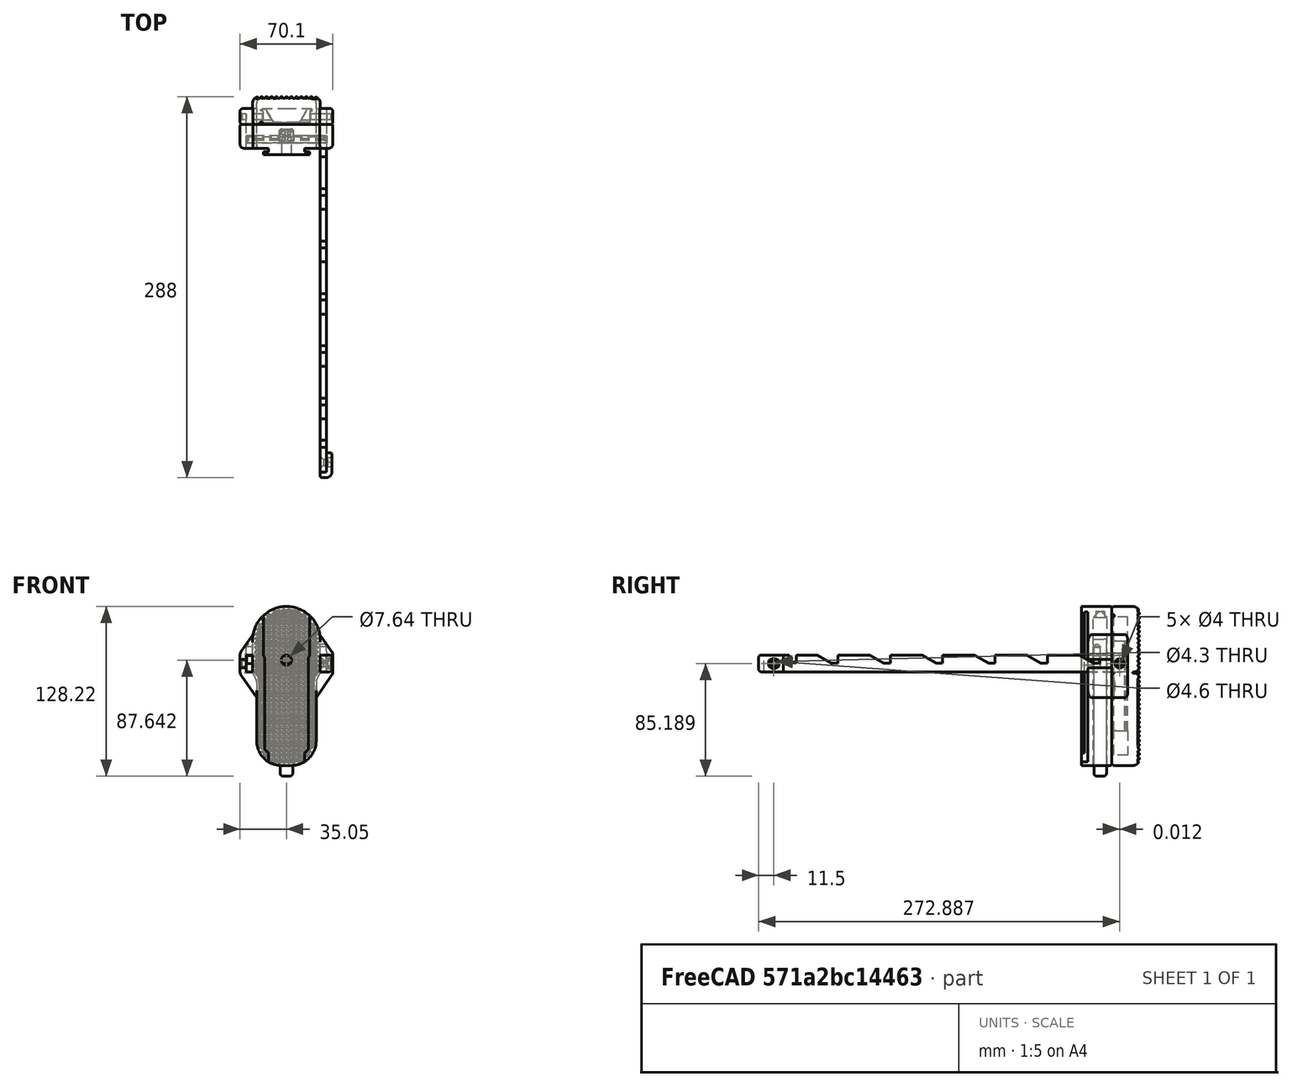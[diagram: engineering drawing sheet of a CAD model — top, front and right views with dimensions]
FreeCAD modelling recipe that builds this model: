
FCSTD DOCUMENT  (FreeCAD 0.19R24291 (Git))
Label: TelescopingButtExtensionMetalArms
License: All rights reserved
LicenseURL: http://en.wikipedia.org/wiki/All_rights_reserved
objects: Sketcher::SketchObject×34, PartDesign::Pocket×20, TechDraw::DrawViewDimension×13, PartDesign::Pad×11, PartDesign::Fillet×10, PartDesign::Body×7, Spreadsheet::Sheet×5, PartDesign::Chamfer×5, PartDesign::Mirrored×4, PartDesign::LinearPattern×3, App::Part×3, Part::Mirroring×2, TechDraw::DrawSVGTemplate×2, TechDraw::DrawViewPart×2, TechDraw::DrawPage×2, PartDesign::SubtractivePipe×1, PartDesign::AdditivePipe×1, PartDesign::Groove×1
note: 148 computed .brp shape members not serialized (recipe doc carries the construction recipe); baked Part::Feature solids carry a one-line shape summary decoded from their .brp

FEATURE [Spreadsheet::Sheet] Spreadsheet  label="P90Measurements"
  cells = A1=ButtDovetail; D1=Overall; G1=ButtPad; I1=Reference Point; J1=Bottom of pad, just at base of dovetail body; L1=SpaceForTelescopingBar; M1(SpaceForTelescopingBar)==0.584"; A2=DovetailHeight; B2(DovetailHeight)==0.192"; D2=ButtOverallHeight; E2(ButtOverallHeight)==4.733"; G2=PadWidestWidth; H2(PadWidestWidth)==2.017"; A3=DovetailBodyWidth; B3(DovetailBodyWidth)==28mm; D3=PadBCGHoleFromReferencePoint; E3(PadBCGHoleFromReferencePoint)==2.997"; G3=PadThinnestWidth; H3(PadThinnestWidth)==1.772"; A4=DovetailLedgeHeight; B4(DovetailLedgeHeight)==0.1"; D4=PadBCGHoleDiameter; E4(PadBCGHoleDiameter)==0.277"; G4=PadWidestWidthInnerShoulderDistanceFromReferencePoint; H4(PadWidestWidthInnerShoulderDistanceFromReferencePoint)==2.532"; A5=DovetailLedgeWidestWidth; B5(DovetailLedgeWidestWidth)==35.5mm; D5=PadBCGHoleDepth; E5(PadBCGHoleDepth)==0.375"; G5=PadWidestWidthOuterShoulderDistanceFromReferencePoint; H5(PadWidestWidthOuterShoulderDistanceFromReferencePoint)==2.785"; A6=DovetailLedgeMiddleWidth; B6(DovetailLedgeMiddleWidth)==1.32"; G6=PadBottomWidth; H6(PadBottomWidth)==0.3"; A7=DovetailMiddleWidthInsideShoulderDistanceFromReferencePoint; B7(DovetailMiddleWidthInsideShoulderDistanceFromReferencePoint)==0.37"; A8=DovetailMiddleWidthOutsideShoulderDistanceFromReferencePoint; B8(DovetailMiddleWidthOutsideShoulderDistanceFromReferencePoint)==0.484"; A9=DovetailBottobBodyBevelDistanceFromReferencePoint; B9(DovetailBottobBodyBevelDistanceFromReferencePoint)==0.154"; A10=DovetailWidestLedgeStartingPointFromReferencePoint; B10(DovetailWidestLedgeStartingPointFromReferencePoint)==3.222"
FEATURE [Spreadsheet::Sheet] Spreadsheet001  label="ProjectSettings"
  cells = A1=Tolerance; A2=LooseTolerance; B2(LooseTolerance)==0.3mm; C2=SpringMaxHeight; D2(SpringMaxHeight)==20mm; E2=CrosspinWidth; F2(CrosspinWidth)==4mm; G2=EndcapScrewBodyDiameter; H2(EndcapScrewBodyDiameter)==4mm; I2=LengthFromButtToChargingHandleShelf; J2(LengthFromButtToChargingHandleShelf)==310mm; K2=AdditionalPrinterTolerance; L2(AdditionalPrinterTolerance)==0mm; A3=TightTolerance; B3(TightTolerance)==0.1mm + AdditionalPrinterTolerance; C3=TelescopingPadOAL; D3(TelescopingPadOAL)==TelescopingBarInsertDepth + TelescopingButtThickness; E3=CrosspinHeight; F3(CrosspinHeight)==6mm; G3=EndcapScrewHeadDiameter; H3(EndcapScrewHeadDiameter)==6mm; A4=WallThickness; B4(WallThickness)==4mm; C4=StandardFillet; D4(StandardFillet)==2mm; E4=CrosspinLength; G4=EndcapNutHeight; H4(EndcapNutHeight)==0.273"; A5=LockingButtonWidth; B5(LockingButtonWidth)==10mm; C5=LockingPinWidth; D5(LockingPinWidth)==0.1875"; E5=ButtonActuationDistance; F5(ButtonActuationDistance)==CrosspinHeight * 2; G5=EndcapNutThickness; H5(EndcapNutThickness)==0.121"; A6=LockingButtonHeight; B6(LockingButtonHeight)==10mm; C6=LockingPinHeight; D6(LockingPinHeight)==6mm; G6=EndcapSectionOnBarLength; H6(EndcapSectionOnBarLength)==15mm; A7=LockingButtonLength; B7(LockingButtonLength)==60mm; C7=LockingPinLength; D7(LockingPinLength)==40mm; G7=EndcapSectionHangingOffOfBarLength; H7(EndcapSectionHangingOffOfBarLength)==WallThickness; A8=LockingButtonHoleDepth; B8(LockingButtonHoleDepth)==<<P90Measurements>>.PadWidestWidthOuterShoulderDistanceFromReferencePoint + BarThickness + LockingPinHeight * 3 + SpringMaxHeight; C8=BarThickness; D8(BarThickness)==0.1875"; G8=ScrewCountersinkDepth; H8(ScrewCountersinkDepth)==0.089"; A9=LockingButtonActuationDistance; B9(LockingButtonActuationDistance)==6mm; C9=BarHeight; D9(BarHeight)==12.7mm; G9=EndcapScrewThreadHeight; H9(EndcapScrewThreadHeight)==8mm; A10=LockingBodyLength; B10(LockingBodyLength)==WallThickness * 2 + LockingButtonHeight; C10=BarLength; D10(BarLength)==275mm; A11=TelescopingPadComfortFilletRadius; B11(TelescopingPadComfortFilletRadius)==5mm; C11=BarNumberOfKnotches; D11(BarNumberOfKnotches)=6; C12=TelescopingBarInsertDepth; D12(TelescopingBarInsertDepth)==WallThickness * 2 + CrosspinWidth; A13=ScallopRadius; B13(ScallopRadius)==1.5mm; C13=TelescopingButtThickness; D13(TelescopingButtThickness)==10mm; A14=DistanceBetweenScallops; B14(DistanceBetweenScallops)==0.25mm; C14=BarDistanceBetweenKnotches; D14(BarDistanceBetweenKnotches)=; C15=BarLastKnotchLocationFromOrigin; D15(BarLastKnotchLocationFromOrigin)==BarLength - EndcapSectionOnBarLength - WallThickness; A16=PaperworkLidNubWidth; B16(PaperworkLidNubWidth)==2mm; C16=BarOccupiedLength; D16(BarOccupiedLength)==WallThickness * 4 + LockingButtonHeight + CrosspinWidth; A17=PaperworkLidNubHeight; B17(PaperworkLidNubHeight)==1.5mm; C17=BarUnoccupiedLength; D17(BarUnoccupiedLength)==BarLength - BarOccupiedLength; A18=PaperworkLidWallThickness; B18(PaperworkLidWallThickness)==2mm; A19=PaperworkLidFingerHoleDiameter; B19(PaperworkLidFingerHoleDiameter)==20mm; A20=PaperworkLipTabWallFilletRadius; B20(PaperworkLipTabWallFilletRadius)==4mm; A21=PaperwokLipInteriorWallAngle; B21(PaperwokLipInteriorWallAngle)=120; A22=PaperworklidbaseThickness; B22(PaperworklidbaseThickness)==1.5mm; A24=LockingButtonHoleClearanceForChamfer; B24(LockingButtonHoleClearanceForChamfer)==min(LockingButtonWidth; LockingButtonHeight) * 9 / 20; A25=LockingPinPocketOverhangCompensationDistance; B25(LockingPinPocketOverhangCompensationDistance)==1.5mm
FEATURE [Sketcher::SketchObject] Sketch  label="DovetailBodySketch"
  FullyConstrained = true
  MapMode = 5
  Placement = pos=(0,0,0) rot=(1,0,0;1.5708rad)
  Support = -> [XZ_Plane]
  expr: Constraints[10] = <<P90Measurements>>.DovetailBodyWidth - <<ProjectSettings>>.LooseTolerance * 2
  expr: Constraints[9] = <<P90Measurements>>.ButtOverallHeight
  sketch-geometry (4):
    g0: LineSegment StartX=-13.7 StartY=120.218 StartZ=0 EndX=13.7 EndY=120.218 EndZ=0
    g1: LineSegment StartX=13.7 StartY=120.218 StartZ=0 EndX=13.7 EndY=0 EndZ=0
    g2: LineSegment StartX=13.7 StartY=0 StartZ=0 EndX=-13.7 EndY=0 EndZ=0
    g3: LineSegment StartX=-13.7 StartY=0 StartZ=0 EndX=-13.7 EndY=120.218 EndZ=0
  constraints (11):
    c: Coincident(g0,g1)
    c: Coincident(g1,g2)
    c: Coincident(g2,g3)
    c: Coincident(g3,g0)
    c: Horizontal(g0)
    c: Vertical(g1)
    c: Vertical(g3)
    c: PointOnObject(g1,g-1)
    c: Symmetric(g1,g2,g-2)
    c: DistanceY(g1,g1) = 120.218
    c: DistanceX(g0,g0) = 27.4
FEATURE [PartDesign::Pad] Pad  label="DovetailBodyPad"
  Direction = (1,1,1)
  Length = 4.8768
  Length2 = 100
  Placement = pos=(0,0,0) rot=(1,0,0;1.5708rad)
  Profile = -> Sketch
  Type = 0
  expr: Length = <<P90Measurements>>.DovetailHeight
FEATURE [Sketcher::SketchObject] Sketch001  label="DovetailLedgeSketch"
  AttachmentOffset = pos=(0,0,4.8768) rot=(0,0,1;0rad)
  FullyConstrained = true
  MapMode = 5
  Placement = pos=(0,-4.8768,-1.1e-15) rot=(1,0,0;1.5708rad)
  Support = -> [XZ_Plane]
  expr: .AttachmentOffset.Base.z = <<P90Measurements>>.DovetailHeight
  expr: Constraints[10] = <<P90Measurements>>.DovetailLedgeWidestWidth - <<ProjectSettings>>.LooseTolerance * 2
  expr: Constraints[9] = <<P90Measurements>>.ButtOverallHeight
  sketch-geometry (4):
    g0: LineSegment StartX=-17.45 StartY=120.218 StartZ=0 EndX=17.45 EndY=120.218 EndZ=0
    g1: LineSegment StartX=17.45 StartY=120.218 StartZ=0 EndX=17.45 EndY=0 EndZ=0
    g2: LineSegment StartX=17.45 StartY=0 StartZ=0 EndX=-17.45 EndY=0 EndZ=0
    g3: LineSegment StartX=-17.45 StartY=0 StartZ=0 EndX=-17.45 EndY=120.218 EndZ=0
  constraints (11):
    c: Coincident(g0,g1)
    c: Coincident(g1,g2)
    c: Coincident(g2,g3)
    c: Coincident(g3,g0)
    c: Horizontal(g0)
    c: Vertical(g1)
    c: Vertical(g3)
    c: PointOnObject(g1,g-1)
    c: Symmetric(g2,g1,g-2)
    c: DistanceY(g1,g1) = 120.218
    c: DistanceX(g0,g0) = 34.9
FEATURE [PartDesign::Pad] Pad001  label="DovetailLedgePad"
  BaseFeature = -> Pad
  Direction = (1,1,1)
  Length = 2.24
  Length2 = 100
  Placement = pos=(0,0,0) rot=(1,0,0;1.5708rad)
  Profile = -> Sketch001
  Refine = true
  Reversed = true
  Type = 0
  expr: Length = <<P90Measurements>>.DovetailLedgeHeight - <<ProjectSettings>>.LooseTolerance
FEATURE [Sketcher::SketchObject] Sketch002  label="DovetailLedgeCutSketch"
  FullyConstrained = true
  MapMode = 5
  Placement = pos=(0,0,0) rot=(1,0,0;1.5708rad)
  Support = -> [XZ_Plane]
  expr: Constraints[35] = <<P90Measurements>>.DovetailMiddleWidthOutsideShoulderDistanceFromReferencePoint
  expr: Constraints[33] = <<P90Measurements>>.DovetailLedgeMiddleWidth - <<ProjectSettings>>.LooseTolerance * 2
  expr: Constraints[36] = <<P90Measurements>>.DovetailWidestLedgeStartingPointFromReferencePoint
  expr: Constraints[34] = <<P90Measurements>>.DovetailMiddleWidthInsideShoulderDistanceFromReferencePoint
  expr: Constraints[32] = <<P90Measurements>>.DovetailBodyWidth - <<ProjectSettings>>.LooseTolerance * 2
  expr: Constraints[29] = <<P90Measurements>>.DovetailLedgeWidestWidth - <<ProjectSettings>>.LooseTolerance * 2
  expr: Constraints[28] = <<P90Measurements>>.ButtOverallHeight
  sketch-geometry (16):
    g0: LineSegment StartX=-27.45 StartY=130.218 StartZ=0 EndX=27.45 EndY=130.218 EndZ=0
    g1: LineSegment StartX=27.45 StartY=130.218 StartZ=0 EndX=27.45 EndY=-10 EndZ=0
    g2: LineSegment StartX=27.45 StartY=-10 StartZ=0 EndX=-27.45 EndY=-10 EndZ=0
    g3: LineSegment StartX=-27.45 StartY=-10 StartZ=0 EndX=-27.45 EndY=130.218 EndZ=0
    g4: LineSegment StartX=-13.7 StartY=0 StartZ=0 EndX=13.7 EndY=0 EndZ=0
    g5: LineSegment StartX=13.7 StartY=0 StartZ=0 EndX=13.7 EndY=9.398 EndZ=0
    g6: LineSegment StartX=13.7 StartY=9.398 StartZ=0 EndX=16.464 EndY=12.2936 EndZ=0
    g7: LineSegment StartX=16.464 StartY=12.2936 StartZ=0 EndX=16.464 EndY=81.8388 EndZ=0
    g8: LineSegment StartX=16.464 StartY=81.8388 StartZ=0 EndX=17.45 EndY=82.8598 EndZ=0
    g9: LineSegment StartX=17.45 StartY=82.8598 StartZ=0 EndX=17.45 EndY=120.218 EndZ=0
    g10: LineSegment StartX=17.45 StartY=120.218 StartZ=0 EndX=-17.45 EndY=120.218 EndZ=0
    g11: LineSegment StartX=-17.45 StartY=120.218 StartZ=0 EndX=-17.45 EndY=82.8598 EndZ=0
    g12: LineSegment StartX=-17.45 StartY=82.8598 StartZ=0 EndX=-16.464 EndY=81.8388 EndZ=0
    g13: LineSegment StartX=-16.464 StartY=81.8388 StartZ=0 EndX=-16.464 EndY=12.2936 EndZ=0
    g14: LineSegment StartX=-16.464 StartY=12.2936 StartZ=0 EndX=-13.7 EndY=9.398 EndZ=0
    g15: LineSegment StartX=-13.7 StartY=9.398 StartZ=0 EndX=-13.7 EndY=0 EndZ=0
  constraints (44):
    c: Coincident(g0,g1)
    c: Coincident(g1,g2)
    c: Coincident(g2,g3)
    c: Coincident(g3,g0)
    c: Horizontal(g0)
    c: Horizontal(g2)
    c: Vertical(g1)
    c: Vertical(g3)
    c: PointOnObject(g4,g-1)
    c: Coincident(g4,g5)
    c: Vertical(g5)
    c: Coincident(g5,g6)
    c: Coincident(g6,g7)
    c: Vertical(g7)
    c: Coincident(g7,g8)
    c: Coincident(g8,g9)
    c: Vertical(g9)
    c: Coincident(g9,g10)
    c: Coincident(g10,g11)
    c: Coincident(g11,g12)
    c: Coincident(g12,g13)
    c: Vertical(g13)
    c: Coincident(g13,g14)
    c: Coincident(g14,g15)
    c: Coincident(g15,g4)
    c: Vertical(g15)
    c: Horizontal(g14,g5)
    c: Horizontal(g13,g6)
    c: DistanceY(g4,g9) = 120.218
    c: DistanceX(g10,g10) = 34.9
    c: Symmetric(g10,g9,g-2)
    c: Symmetric(g12,g7,g-2)
    c: DistanceX(g4,g4) = 27.4
    c: DistanceX(g12,g7) = 32.928
    c: DistanceY(g14) = 9.398
    c: DistanceY(g4,g13) = 12.2936
    c: DistanceY(g-1,g7) = 81.8388
    c: DistanceY(g10,g0) = 10
    c: DistanceX(g0,g10) = 10
    c: DistanceX(g9,g1) = 10
    c: DistanceY(g1,g4) = 10
    c: Symmetric(g4,g4,g-2)
    c: Symmetric(g8,g11,g-2)
    c: Angle(g12,g13) = 2.37365
FEATURE [PartDesign::Pocket] Pocket  label="DovetailLedgeCutPocket"
  BaseFeature = -> Pad001
  Length = 5
  Length2 = 100
  Placement = pos=(0,0,0) rot=(1,0,0;1.5708rad)
  Profile = -> Sketch002
  Reversed = true
  Type = 1
FEATURE [Sketcher::SketchObject] Sketch003  label="PadBodySketch"
  FullyConstrained = true
  MapMode = 5
  Placement = pos=(0,0,0) rot=(1,0,0;1.5708rad)
  Support = -> [XZ_Plane]
  expr: Constraints[27] = <<P90Measurements>>.PadWidestWidthInnerShoulderDistanceFromReferencePoint
  expr: Constraints[22] = <<P90Measurements>>.PadWidestWidthOuterShoulderDistanceFromReferencePoint
  expr: Constraints[19] = <<P90Measurements>>.PadThinnestWidth
  expr: Constraints[21] = <<P90Measurements>>.PadWidestWidth
  expr: Constraints[20] = <<P90Measurements>>.ButtOverallHeight
  sketch-geometry (12):
    g0: LineSegment StartX=-22.5044 StartY=0 StartZ=0 EndX=22.5044 EndY=0 EndZ=0
    g1: LineSegment StartX=22.5044 StartY=0 StartZ=0 EndX=22.5044 EndY=63.2152 EndZ=0
    g2: LineSegment StartX=-22.5044 StartY=63.2152 StartZ=0 EndX=-22.5044 EndY=0 EndZ=0
    g3: LineSegment StartX=-25.6159 StartY=120.218 StartZ=0 EndX=25.6159 EndY=120.218 EndZ=0
    g4: LineSegment StartX=25.6159 StartY=120.218 StartZ=0 EndX=25.6159 EndY=70.739 EndZ=0
    g5: LineSegment StartX=-25.6159 StartY=70.739 StartZ=0 EndX=-25.6159 EndY=120.218 EndZ=0
    g6: LineSegment StartX=-25.3621 StartY=69.6414 StartZ=0 EndX=-22.7582 EndY=64.3128 EndZ=0
    g7: LineSegment StartX=25.3621 StartY=69.6414 StartZ=0 EndX=22.7582 EndY=64.3128 EndZ=0
    g8: ArcOfCircle CenterX=-23.1159 CenterY=70.739 CenterZ=0 NormalX=0 NormalY=0 NormalZ=1 AngleXU=0 Radius=2.5 StartAngle=3.14159 EndAngle=3.59612
    g9: ArcOfCircle CenterX=-25.0044 CenterY=63.2152 CenterZ=0 NormalX=0 NormalY=0 NormalZ=1 AngleXU=0 Radius=2.5 StartAngle=2e-16 EndAngle=0.454529
    g10: ArcOfCircle CenterX=23.1159 CenterY=70.739 CenterZ=0 NormalX=0 NormalY=0 NormalZ=1 AngleXU=0 Radius=2.5 StartAngle=5.82866 EndAngle=6.28319
    g11: ArcOfCircle CenterX=25.0044 CenterY=63.2152 CenterZ=0 NormalX=0 NormalY=0 NormalZ=1 AngleXU=0 Radius=2.5 StartAngle=2.68706 EndAngle=3.14159
  constraints (28):
    c: Coincident(g0,g1)
    c: Coincident(g2,g0)
    c: Vertical(g1)
    c: Vertical(g2)
    c: PointOnObject(g0,g-1)
    c: Coincident(g3,g4)
    c: Coincident(g5,g3)
    c: Vertical(g4)
    c: Vertical(g5)
    c: Tangent(g8,g5) = 1.5708
    c: Tangent(g8,g6) = -1.5708
    c: Tangent(g9,g6) = 1.5708
    c: Tangent(g11,g1) = 1.5708
    c: Tangent(g11,g7) = -1.5708
    c: Tangent(g7,g10) = 1.5708
    c: Tangent(g10,g4) = 1.5708
    c: Tangent(g9,g2) = 1.5708
    c: Symmetric(g0,g0,g-2)
    c: Symmetric(g3,g3,g-2)
    c: DistanceX(g0,g0) = 45.0088
    c: DistanceY(g0,g3) = 120.218
    c: DistanceX(g3,g3) = 51.2318
    c: DistanceY(g-1,g8) = 70.739
    c: Symmetric(g7,g6,g-2)
    c: Symmetric(g6,g7,g-2)
    c: Equal(g11,g10)
    c: Diameter(g11) = 5
    c: DistanceY(g6) = 64.3128
FEATURE [PartDesign::Pad] Pad002  label="PadBodyPad"
  BaseFeature = -> Pocket
  Direction = (1,1,1)
  Length = 18
  Length2 = 100
  Placement = pos=(0,0,0) rot=(1,0,0;1.5708rad)
  Profile = -> Sketch003
  Reversed = true
  Type = 0
  expr: Length = <<ProjectSettings>>.WallThickness * 2 + <<ProjectSettings>>.LockingButtonHeight
FEATURE [Sketcher::SketchObject] Sketch004  label="PadBevelsCutSketch"
  FullyConstrained = true
  MapMode = 5
  Placement = pos=(0,0,0) rot=(1,0,0;1.5708rad)
  Support = -> [XZ_Plane]
  expr: Constraints[32] = <<P90Measurements>>.PadBottomWidth
  expr: Constraints[29] = <<P90Measurements>>.PadWidestWidth
  expr: Constraints[31] = <<P90Measurements>>.PadWidestWidthInnerShoulderDistanceFromReferencePoint - 5mm
  expr: Constraints[30] = <<P90Measurements>>.PadThinnestWidth
  expr: Constraints[27] = <<P90Measurements>>.ButtOverallHeight
  sketch-geometry (15):
    g0: LineSegment StartX=-35.6159 StartY=130.218 StartZ=0 EndX=35.6159 EndY=130.218 EndZ=0
    g1: LineSegment StartX=35.6159 StartY=130.218 StartZ=0 EndX=35.6159 EndY=-10 EndZ=0
    g2: LineSegment StartX=35.6159 StartY=-10 StartZ=0 EndX=-35.6159 EndY=-10 EndZ=0
    g3: LineSegment StartX=-35.6159 StartY=-10 StartZ=0 EndX=-35.6159 EndY=130.218 EndZ=0
    g4: ArcOfCircle CenterX=-3.81 CenterY=18.6944 CenterZ=0 NormalX=0 NormalY=0 NormalZ=1 AngleXU=0 Radius=18.6944 StartAngle=3.14159 EndAngle=4.71239
    g5: ArcOfCircle CenterX=3.81 CenterY=18.6944 CenterZ=0 NormalX=0 NormalY=0 NormalZ=1 AngleXU=0 Radius=18.6944 StartAngle=4.71239 EndAngle=6.28319
    g6: ArcOfCircle CenterX=2.5e-15 CenterY=94.6023 CenterZ=0 NormalX=0 NormalY=0 NormalZ=1 AngleXU=0 Radius=25.6159 StartAngle=1.5708 EndAngle=3.14159
    g7: ArcOfCircle CenterX=2.5e-15 CenterY=94.6023 CenterZ=0 NormalX=0 NormalY=0 NormalZ=1 AngleXU=0 Radius=25.6159 StartAngle=0 EndAngle=1.5708
    g8: LineSegment StartX=-25.6159 StartY=94.6023 StartZ=0 EndX=-25.6159 EndY=59.3128 EndZ=0
    g9: LineSegment StartX=-25.6159 StartY=59.3128 StartZ=0 EndX=-22.5044 EndY=59.3128 EndZ=0
    g10: LineSegment StartX=-22.5044 StartY=59.3128 StartZ=0 EndX=-22.5044 EndY=18.6944 EndZ=0
    g11: LineSegment StartX=-3.81 StartY=0 StartZ=0 EndX=3.81 EndY=0 EndZ=0
    g12: LineSegment StartX=22.5044 StartY=18.6944 StartZ=0 EndX=22.5044 EndY=59.3128 EndZ=0
    g13: LineSegment StartX=22.5044 StartY=59.3128 StartZ=0 EndX=25.6159 EndY=59.3128 EndZ=0
    g14: LineSegment StartX=25.6159 StartY=59.3128 StartZ=0 EndX=25.6159 EndY=94.6023 EndZ=0
  constraints (39):
    c: Coincident(g0,g1)
    c: Coincident(g1,g2)
    c: Coincident(g2,g3)
    c: Coincident(g3,g0)
    c: Horizontal(g0)
    c: Vertical(g1)
    c: Vertical(g3)
    c: Symmetric(g2,g1,g-2)
    c: PointOnObject(g4,g-1)
    c: PointOnObject(g5,g-1)
    c: Vertical(g8)
    c: Coincident(g9,g8)
    c: Vertical(g10)
    c: Vertical(g12)
    c: Coincident(g13,g12)
    c: Vertical(g14)
    c: Coincident(g13,g14)
    c: Horizontal(g13)
    c: Tangent(g6,g8) = -1.5708
    c: Tangent(g7,g14) = -1.5708
    c: Tangent(g10,g4) = -1.5708
    c: Tangent(g11,g4) = -1.5708
    c: Tangent(g11,g5) = -1.5708
    c: Tangent(g12,g5) = -1.5708
    c: Symmetric(g12,g10,g-2)
    c: Symmetric(g8,g13,g-2)
    c: Coincident(g10,g9)
    c: DistanceY(g-1,g7) = 120.218
    c: Equal(g5,g4)
    c: DistanceX(g6,g7) = 51.2318
    c: DistanceX(g9,g12) = 45.0088
    c: DistanceY(g-1,g12) = 59.3128
    c: DistanceX(g11,g11) = 7.62
    c: PointOnObject(g6,g-2)
    c: Tangent(g6,g7) = -1.5708
    c: Equal(g8,g14)
    c: DistanceY(g2,g-1) = 10
    c: DistanceY(g6,g0) = 10
    c: DistanceX(g7,g1) = 10
FEATURE [PartDesign::Pocket] Pocket001  label="PadBevelsCutPocket"
  BaseFeature = -> Pad002
  Length = 5
  Length2 = 100
  Midplane = true
  Placement = pos=(0,0,0) rot=(1,0,0;1.5708rad)
  Profile = -> Sketch004
  Type = 1
FEATURE [Spreadsheet::Sheet] Spreadsheet002  label="TelescopingBarSettings"
  cells = A1=BarOffsetFromCenter; B1(BarOffsetFromCenter)==<<PadBodyPad>>.Length + <<TelescoptingPadBodyPad>>.Length; A2=LengthFromButtToChargingHandleShelf; B2(LengthFromButtToChargingHandleShelf)==310mm; A3=BarLength; B3(BarLength)==270mm; A4=BarThickness; B4(BarThickness)==0.125"; A5=CrosspinThickness; B5(CrosspinThickness)==0.125"; A6=BarHeight; B6(BarHeight)==12.7mm; A7=LockingPinThickness; B7(LockingPinThickness)==0.125"; A8=BarNumberOfKnotches; B8(BarNumberOfKnotches)=6; A9=ScrewCountersinkDepth; B9(ScrewCountersinkDepth)==0.089"; A10=EndcapHexnutHeight; B10(EndcapHexnutHeight)==0.273"; A11=EndcapHexnutThickness; B11(EndcapHexnutThickness)==0.121"; A12=CrosspinHeight; B12(CrosspinHeight)==6mm; A13=LockingPinHeight; B13(LockingPinHeight)==6mm
FEATURE [Sketcher::SketchObject] Sketch008  label="TelescoptingPadBodySketch"
  FullyConstrained = true
  MapMode = 5
  Placement = pos=(0,0,0) rot=(1,0,0;1.5708rad)
  Support = -> [XZ_Plane002]
  expr: Constraints[20] = <<P90Measurements>>.ButtOverallHeight
  expr: Constraints[21] = <<P90Measurements>>.PadWidestWidth
  expr: Constraints[19] = <<P90Measurements>>.PadThinnestWidth
  expr: Constraints[22] = <<P90Measurements>>.PadWidestWidthOuterShoulderDistanceFromReferencePoint
  expr: Constraints[27] = <<P90Measurements>>.PadWidestWidthInnerShoulderDistanceFromReferencePoint
  sketch-geometry (12):
    g0: LineSegment StartX=-22.5044 StartY=0 StartZ=0 EndX=22.5044 EndY=0 EndZ=0
    g1: LineSegment StartX=22.5044 StartY=0 StartZ=0 EndX=22.5044 EndY=63.2152 EndZ=0
    g2: LineSegment StartX=-22.5044 StartY=63.2152 StartZ=0 EndX=-22.5044 EndY=0 EndZ=0
    g3: LineSegment StartX=-25.6159 StartY=120.218 StartZ=0 EndX=25.6159 EndY=120.218 EndZ=0
    g4: LineSegment StartX=25.6159 StartY=120.218 StartZ=0 EndX=25.6159 EndY=70.739 EndZ=0
    g5: LineSegment StartX=-25.6159 StartY=70.739 StartZ=0 EndX=-25.6159 EndY=120.218 EndZ=0
    g6: LineSegment StartX=-25.3621 StartY=69.6414 StartZ=0 EndX=-22.7582 EndY=64.3128 EndZ=0
    g7: LineSegment StartX=25.3621 StartY=69.6414 StartZ=0 EndX=22.7582 EndY=64.3128 EndZ=0
    g8: ArcOfCircle CenterX=-23.1159 CenterY=70.739 CenterZ=0 NormalX=0 NormalY=0 NormalZ=1 AngleXU=0 Radius=2.5 StartAngle=3.14159 EndAngle=3.59612
    g9: ArcOfCircle CenterX=-25.0044 CenterY=63.2152 CenterZ=0 NormalX=0 NormalY=0 NormalZ=1 AngleXU=0 Radius=2.5 StartAngle=0 EndAngle=0.454529
    g10: ArcOfCircle CenterX=23.1159 CenterY=70.739 CenterZ=0 NormalX=0 NormalY=0 NormalZ=1 AngleXU=0 Radius=2.5 StartAngle=5.82866 EndAngle=6.28319
    g11: ArcOfCircle CenterX=25.0044 CenterY=63.2152 CenterZ=0 NormalX=0 NormalY=0 NormalZ=1 AngleXU=0 Radius=2.5 StartAngle=2.68706 EndAngle=3.14159
  constraints (29):
    c: Coincident(g0,g1)
    c: Coincident(g2,g0)
    c: Vertical(g1)
    c: Vertical(g2)
    c: PointOnObject(g0,g-1)
    c: Coincident(g3,g4)
    c: Coincident(g5,g3)
    c: Vertical(g4)
    c: Vertical(g5)
    c: Tangent(g8,g5) = 1.5708
    c: Tangent(g8,g6) = -1.5708
    c: Tangent(g9,g6) = 1.5708
    c: Tangent(g11,g1) = 1.5708
    c: Tangent(g11,g7) = -1.5708
    c: Tangent(g7,g10) = 1.5708
    c: Tangent(g10,g4) = 1.5708
    c: Tangent(g9,g2) = 1.5708
    c: Symmetric(g0,g0,g-2)
    c: Symmetric(g3,g3,g-2)
    c: DistanceX(g0,g0) = 45.0088
    c: DistanceY(g0,g3) = 120.218
    c: DistanceX(g3,g3) = 51.2318
    c: DistanceY(g-1,g8) = 70.739
    c: Symmetric(g7,g6,g-2)
    c: Symmetric(g6,g7,g-2)
    c: Equal(g11,g10)
    c: Diameter(g11) = 5
    c: DistanceY(g6) = 64.3128
    c: Angle(g1,g7) = 2.68706  'PadAngle'
FEATURE [PartDesign::Pad] Pad006  label="TelescoptingPadBodyPad"
  Direction = (1,1,1)
  Length = 21
  Length2 = 100
  Placement = pos=(0,0,0) rot=(1,0,0;1.5708rad)
  Profile = -> Sketch008
  Reversed = true
  Type = 0
  expr: Length = <<ProjectSettings>>.TelescopingBarInsertDepth + <<ProjectSettings>>.WallThickness + <<ProjectSettings>>.TelescopingPadComfortFilletRadius
FEATURE [Sketcher::SketchObject] Sketch009  label="TelescopingPadBevelsCutSketch"
  FullyConstrained = true
  MapMode = 5
  Placement = pos=(0,0,0) rot=(1,0,0;1.5708rad)
  Support = -> [XZ_Plane002]
  expr: Constraints[27] = <<P90Measurements>>.ButtOverallHeight
  expr: Constraints[30] = <<P90Measurements>>.PadThinnestWidth
  expr: Constraints[31] = <<P90Measurements>>.PadWidestWidthInnerShoulderDistanceFromReferencePoint - 5mm
  expr: Constraints[29] = <<P90Measurements>>.PadWidestWidth
  expr: Constraints[32] = <<P90Measurements>>.PadBottomWidth
  sketch-geometry (15):
    g0: LineSegment StartX=-35.6159 StartY=130.218 StartZ=0 EndX=35.6159 EndY=130.218 EndZ=0
    g1: LineSegment StartX=35.6159 StartY=130.218 StartZ=0 EndX=35.6159 EndY=-10 EndZ=0
    g2: LineSegment StartX=35.6159 StartY=-10 StartZ=0 EndX=-35.6159 EndY=-10 EndZ=0
    g3: LineSegment StartX=-35.6159 StartY=-10 StartZ=0 EndX=-35.6159 EndY=130.218 EndZ=0
    g4: ArcOfCircle CenterX=-3.81 CenterY=18.6944 CenterZ=0 NormalX=0 NormalY=0 NormalZ=1 AngleXU=0 Radius=18.6944 StartAngle=3.14159 EndAngle=4.71239
    g5: ArcOfCircle CenterX=3.81 CenterY=18.6944 CenterZ=0 NormalX=0 NormalY=0 NormalZ=1 AngleXU=0 Radius=18.6944 StartAngle=4.71239 EndAngle=6.28319
    g6: ArcOfCircle CenterX=8e-16 CenterY=94.6023 CenterZ=0 NormalX=0 NormalY=0 NormalZ=1 AngleXU=0 Radius=25.6159 StartAngle=1.5708 EndAngle=3.14159
    g7: ArcOfCircle CenterX=8e-16 CenterY=94.6023 CenterZ=0 NormalX=0 NormalY=0 NormalZ=1 AngleXU=0 Radius=25.6159 StartAngle=0 EndAngle=1.5708
    g8: LineSegment StartX=-25.6159 StartY=94.6023 StartZ=0 EndX=-25.6159 EndY=59.3128 EndZ=0
    g9: LineSegment StartX=-25.6159 StartY=59.3128 StartZ=0 EndX=-22.5044 EndY=59.3128 EndZ=0
    g10: LineSegment StartX=-22.5044 StartY=59.3128 StartZ=0 EndX=-22.5044 EndY=18.6944 EndZ=0
    g11: LineSegment StartX=-3.81 StartY=0 StartZ=0 EndX=3.81 EndY=0 EndZ=0
    g12: LineSegment StartX=22.5044 StartY=18.6944 StartZ=0 EndX=22.5044 EndY=59.3128 EndZ=0
    g13: LineSegment StartX=22.5044 StartY=59.3128 StartZ=0 EndX=25.6159 EndY=59.3128 EndZ=0
    g14: LineSegment StartX=25.6159 StartY=59.3128 StartZ=0 EndX=25.6159 EndY=94.6023 EndZ=0
  constraints (39):
    c: Coincident(g0,g1)
    c: Coincident(g1,g2)
    c: Coincident(g2,g3)
    c: Coincident(g3,g0)
    c: Horizontal(g0)
    c: Vertical(g1)
    c: Vertical(g3)
    c: Symmetric(g2,g1,g-2)
    c: PointOnObject(g4,g-1)
    c: PointOnObject(g5,g-1)
    c: Vertical(g8)
    c: Coincident(g9,g8)
    c: Vertical(g10)
    c: Vertical(g12)
    c: Coincident(g13,g12)
    c: Vertical(g14)
    c: Coincident(g13,g14)
    c: Horizontal(g13)
    c: Tangent(g6,g8) = -1.5708
    c: Tangent(g7,g14) = -1.5708
    c: Tangent(g10,g4) = -1.5708
    c: Tangent(g11,g4) = -1.5708
    c: Tangent(g11,g5) = -1.5708
    c: Tangent(g12,g5) = -1.5708
    c: Symmetric(g12,g10,g-2)
    c: Symmetric(g8,g13,g-2)
    c: Coincident(g10,g9)
    c: DistanceY(g-1,g7) = 120.218
    c: Equal(g5,g4)
    c: DistanceX(g6,g7) = 51.2318
    c: DistanceX(g9,g12) = 45.0088
    c: DistanceY(g-1,g12) = 59.3128
    c: DistanceX(g11,g11) = 7.62
    c: PointOnObject(g6,g-2)
    c: Tangent(g6,g7) = -1.5708
    c: Equal(g8,g14)
    c: DistanceY(g2,g-1) = 10
    c: DistanceY(g6,g0) = 10
    c: DistanceX(g7,g1) = 10
FEATURE [PartDesign::Pocket] Pocket002  label="TelescopingPadBevelsCutPocket"
  BaseFeature = -> Pad006
  Length = 5
  Length2 = 100
  Midplane = true
  Placement = pos=(0,0,0) rot=(1,0,0;1.5708rad)
  Profile = -> Sketch009
  Type = 1
FEATURE [Sketcher::SketchObject] Sketch010  label="TelescopingBarInsertArmSketch"
  FullyConstrained = true
  MapMode = 5
  Placement = pos=(0,0,0) rot=(1,0,0;1.5708rad)
  Support = -> [XZ_Plane002]
  expr: Constraints[15] = <<P90Measurements>>.PadThinnestWidth / 2
  expr: Constraints[13] = <<ProjectSettings>>.BarHeight + <<ProjectSettings>>.TightTolerance
  expr: Constraints[10] = <<P90Measurements>>.PadWidestWidth / 2
  expr: Constraints[12] = <<P90Measurements>>.PadWidestWidthOuterShoulderDistanceFromReferencePoint
  expr: Constraints[11] = <<ProjectSettings>>.BarThickness + <<ProjectSettings>>.TightTolerance
  sketch-geometry (10):
    g0: LineSegment StartX=30.4784 StartY=70.739 StartZ=0 EndX=30.4784 EndY=83.539 EndZ=0
    g1: LineSegment StartX=30.4784 StartY=83.539 StartZ=0 EndX=25.6159 EndY=83.539 EndZ=0
    g2: LineSegment StartX=25.6159 StartY=83.539 StartZ=0 EndX=25.6159 EndY=70.739 EndZ=0
    g3: LineSegment StartX=25.6159 StartY=70.739 StartZ=0 EndX=30.4784 EndY=70.739 EndZ=0
    g4: LineSegment StartX=35.0484 StartY=70.739 StartZ=0 EndX=35.0484 EndY=83.639 EndZ=0
    g5: LineSegment StartX=22.5044 StartY=102.995 StartZ=0 EndX=22.5044 EndY=51.3834 EndZ=0
    g6: ArcOfCircle CenterX=30.4784 CenterY=70.739 CenterZ=0 NormalX=0 NormalY=0 NormalZ=1 AngleXU=0 Radius=4.57 StartAngle=5.67232 EndAngle=6.28319
    g7: LineSegment StartX=22.5044 StartY=51.3834 StartZ=0 EndX=34.2219 EndY=68.1178 EndZ=0
    g8: LineSegment StartX=22.5044 StartY=102.995 StartZ=0 EndX=34.2219 EndY=86.2602 EndZ=0
    g9: ArcOfCircle CenterX=30.4784 CenterY=83.639 CenterZ=0 NormalX=0 NormalY=0 NormalZ=1 AngleXU=0 Radius=4.57 StartAngle=-9e-16 EndAngle=0.610865
  constraints (28):
    c: Vertical(g0)
    c: Coincident(g0,g1)
    c: Horizontal(g1)
    c: Coincident(g1,g2)
    c: Vertical(g2)
    c: Coincident(g2,g3)
    c: Coincident(g3,g0)
    c: Vertical(g5)
    c: Vertical(g4)
    c: Horizontal(g3)
    c: DistanceX(g-1,g2) = 25.6159
    c: DistanceX(g1,g1) = 4.8625
    c: DistanceY(g-1,g2) = 70.739
    c: DistanceY(g0,g0) = 12.8
    c: Coincident(g6,g0)
    c: DistanceX(g-1,g5) = 22.5044
    c: Coincident(g7,g5)
    c: Coincident(g8,g5)
    c: Tangent(g6,g4) = -1.5708
    c: Tangent(g7,g6) = -1.5708
    c: Equal(g7,g8)
    c: Angle(g4,g7) = 2.53073
    c: DistanceX(g-1,g4) = 35.0484  'DistanceFromCenterlineToOutsideOfBarInsertArm'
    c: PointOnObject(g9,g0)
    c: DistanceY(g0,g9) = 0.1
    c: Tangent(g9,g8) = 1.5708
    c: Tangent(g9,g4) = -1.5708
    c: Diameter(g9) = 9.14
FEATURE [Spreadsheet::Sheet] Spreadsheet003  label="TelescopingPadSettings"
  cells = A1=TelescopingBarInsertDepth; B1(TelescopingBarInsertDepth)==<<ProjectSettings>>.WallThickness * 2 + <<TelescopingBarSettings>>.CrosspinThickness + <<ProjectSettings>>.TightTolerance * 2; A2=TelescopingButtThickness; B2(TelescopingButtThickness)==10mm; A3=TelescopingPadOAL; B3(TelescopingPadOAL)==TelescopingBarInsertDepth + TelescopingButtThickness
FEATURE [PartDesign::Pad] Pad007  label="TelescopingBarInsertArmPad"
  BaseFeature = -> Pocket002
  Direction = (1,1,1)
  Length = 12
  Length2 = 100
  Placement = pos=(0,0,0) rot=(1,0,0;1.5708rad)
  Profile = -> Sketch010
  Reversed = true
  Type = 0
  expr: Length = <<ProjectSettings>>.TelescopingBarInsertDepth
FEATURE [Sketcher::SketchObject] Sketch011  label="CrosspinHoleSketch"
  FullyConstrained = true
  MapMode = 5
  Placement = pos=(0,0,0) rot=(0.57735,0.57735,0.57735;2.0944rad)
  Support = -> [YZ_Plane002]
  expr: Constraints[2] = <<ProjectSettings>>.CrosspinWidth
  expr: Constraints[0] = <<P90Measurements>>.PadWidestWidthOuterShoulderDistanceFromReferencePoint + <<ProjectSettings>>.BarHeight / 2 + <<ProjectSettings>>.TightTolerance
  expr: Constraints[1] = <<TelescopingPadSettings>>.TelescopingBarInsertDepth / 2 + <<ProjectSettings>>.TightTolerance * 2
  sketch-geometry (1):
    g0: Circle CenterX=5.8875 CenterY=77.189 CenterZ=0 NormalX=0 NormalY=0 NormalZ=1 AngleXU=0 Radius=2
  constraints (3):
    c: DistanceY(g-1,g0) = 77.189
    c: DistanceX(g-1,g0) = 5.8875
    c: Diameter(g0) = 4
FEATURE [PartDesign::Mirrored] Mirrored  label="TelescopingBarInsertArmMirror"
  BaseFeature = -> Pad007
  MirrorPlane = -> Sketch010 [V_Axis]
  Originals = -> [Pad007]
  Placement = pos=(0,0,0) rot=(1,0,0;1.5708rad)
FEATURE [PartDesign::Pocket] Pocket003  label="CrosspinHolePocket"
  BaseFeature = -> Mirrored
  Length = 5
  Length2 = 100
  Midplane = true
  Placement = pos=(0,0,0) rot=(1,0,0;1.5708rad)
  Profile = -> Sketch011
  Type = 1
FEATURE [PartDesign::Fillet] Fillet  label="ComfortFillet"
  Base = -> Pocket003 [Edge59]
  BaseFeature = -> Pocket003
  Placement = pos=(0,0,0) rot=(1,0,0;1.5708rad)
  Radius = 5
  SupportTransform = false
  expr: Radius = <<ProjectSettings>>.TelescopingPadComfortFilletRadius
FEATURE [Spreadsheet::Sheet] Spreadsheet004  label="CentralPadSettings"
  cells = A1=PadThickness; B1(PadThickness)==<<PadBodyPad>>.Length; A2=LockingButtonHoleDepth; B2(LockingButtonHoleDepth)==<<P90Measurements>>.PadWidestWidthOuterShoulderDistanceFromReferencePoint + <<TelescopingBarSettings>>.BarThickness + <<TelescopingBarSettings>>.LockingPinHeight * 3 + SpringMaxHeight; A3=SpringMaxHeight; B3(SpringMaxHeight)==20mm
FEATURE [Sketcher::SketchObject] Sketch014  label="CentralPadTelescopingBarInsertArmSketch"
  FullyConstrained = true
  MapMode = 5
  Placement = pos=(0,0,0) rot=(1,0,0;1.5708rad)
  Support = -> [XZ_Plane]
  expr: Constraints[11] = <<ProjectSettings>>.BarThickness + <<ProjectSettings>>.TightTolerance
  expr: Constraints[12] = <<P90Measurements>>.PadWidestWidthOuterShoulderDistanceFromReferencePoint
  expr: Constraints[10] = <<P90Measurements>>.PadWidestWidth / 2
  expr: Constraints[13] = <<ProjectSettings>>.BarHeight + <<ProjectSettings>>.TightTolerance
  expr: Constraints[16] = <<P90Measurements>>.PadThinnestWidth / 2
  expr: Constraints[34] = <<ProjectSettings>>.LockingPinHeight + <<ProjectSettings>>.TightTolerance * 2
  sketch-geometry (14):
    g0: LineSegment StartX=30.4784 StartY=70.739 StartZ=0 EndX=30.4784 EndY=74.039 EndZ=0
    g1: LineSegment StartX=30.4784 StartY=83.539 StartZ=0 EndX=25.6159 EndY=83.539 EndZ=0
    g2: LineSegment StartX=25.6159 StartY=83.539 StartZ=0 EndX=25.6159 EndY=70.739 EndZ=0
    g3: LineSegment StartX=25.6159 StartY=70.739 StartZ=0 EndX=30.4784 EndY=70.739 EndZ=0
    g4: LineSegment StartX=35.0484 StartY=70.739 StartZ=0 EndX=35.0484 EndY=74.039 EndZ=0
    g5: LineSegment StartX=22.5044 StartY=102.895 StartZ=0 EndX=22.5044 EndY=51.3834 EndZ=0
    g6: ArcOfCircle CenterX=30.4784 CenterY=83.539 CenterZ=0 NormalX=0 NormalY=0 NormalZ=1 AngleXU=0 Radius=4.57 StartAngle=1.6e-14 EndAngle=0.610865
    g7: ArcOfCircle CenterX=30.4784 CenterY=70.739 CenterZ=0 NormalX=0 NormalY=0 NormalZ=1 AngleXU=0 Radius=4.57 StartAngle=5.67232 EndAngle=6.28319
    g8: LineSegment StartX=22.5044 StartY=51.3834 StartZ=0 EndX=34.2219 EndY=68.1178 EndZ=0
    g9: LineSegment StartX=22.5044 StartY=102.895 StartZ=0 EndX=34.2219 EndY=86.1602 EndZ=0
    g10: LineSegment StartX=30.4784 StartY=80.239 StartZ=0 EndX=35.0484 EndY=80.239 EndZ=0
    g11: LineSegment StartX=30.4784 StartY=74.039 StartZ=0 EndX=35.0484 EndY=74.039 EndZ=0
    g12: LineSegment StartX=30.4784 StartY=80.239 StartZ=0 EndX=30.4784 EndY=83.539 EndZ=0
    g13: LineSegment StartX=35.0484 StartY=80.239 StartZ=0 EndX=35.0484 EndY=83.539 EndZ=0
  constraints (37):
    c: Vertical(g0)
    c: Coincident(g12,g1)
    c: Horizontal(g1)
    c: Coincident(g1,g2)
    c: Vertical(g2)
    c: Coincident(g2,g3)
    c: Coincident(g3,g0)
    c: Vertical(g5)
    c: Vertical(g4)
    c: Horizontal(g3)
    c: DistanceX(g-1,g2) = 25.6159
    c: DistanceX(g1,g1) = 4.8625
    c: DistanceY(g-1,g2) = 70.739
    c: DistanceY(g0,g12) = 12.8
    c: Coincident(g6,g12)
    c: Coincident(g7,g0)
    c: DistanceX(g-1,g5) = 22.5044
    c: Coincident(g8,g5)
    c: Coincident(g9,g5)
    c: Tangent(g7,g4) = -1.5708
    c: Tangent(g9,g6) = 1.5708
    c: Tangent(g8,g7) = -1.5708
    c: Diameter(g6) = 9.14
    c: Equal(g8,g9)
    c: Angle(g4,g8) = 2.53073
    c: Horizontal(g11)
    c: Horizontal(g10)
    c: Coincident(g0,g11)
    c: Coincident(g12,g10)
    c: Tangent(g0,g12)
    c: Coincident(g4,g11)
    c: Coincident(g13,g10)
    c: Tangent(g4,g13)
    c: Tangent(g6,g13) = -1.5708
    c: DistanceY(g4,g10) = 6.2
    c: Equal(g12,g0)
    c: Angle(g5,g9) = 0.610865  'BarArmAngle'
FEATURE [PartDesign::Pad] Pad008  label="CentralPadTelescopingBarInsertArmPad"
  BaseFeature = -> Pocket001
  Direction = (1,1,1)
  Length = 18
  Length2 = 100
  Placement = pos=(0,0,0) rot=(1,0,0;1.5708rad)
  Profile = -> Sketch014
  Reversed = true
  Type = 0
  expr: Length = <<CentralPadSettings>>.PadThickness
FEATURE [PartDesign::Mirrored] Mirrored001  label="CentralPadTelescopingBarInsertArmMirror"
  BaseFeature = -> Pad008
  MirrorPlane = -> Sketch014 [V_Axis]
  Originals = -> [Pad008]
  Placement = pos=(0,0,0) rot=(1,0,0;1.5708rad)
FEATURE [Sketcher::SketchObject] Sketch017  label="LockingPinBodySketch"
  FullyConstrained = true
  MapMode = 5
  Placement = pos=(0,0,0) rot=(0.57735,0.57735,0.57735;2.0944rad)
  Support = -> [YZ_Plane005]
  expr: Constraints[9] = <<ProjectSettings>>.LockingPinHeight
  expr: Constraints[6] = <<ProjectSettings>>.LockingPinWidth
  sketch-geometry (4):
    g0: LineSegment StartX=-2.38125 StartY=3 StartZ=0 EndX=2.38125 EndY=3 EndZ=0
    g1: LineSegment StartX=2.38125 StartY=3 StartZ=0 EndX=2.38125 EndY=-3 EndZ=0
    g2: LineSegment StartX=2.38125 StartY=-3 StartZ=0 EndX=-2.38125 EndY=-3 EndZ=0
    g3: LineSegment StartX=-2.38125 StartY=-3 StartZ=0 EndX=-2.38125 EndY=3 EndZ=0
  constraints (10):
    c: Coincident(g0,g1)
    c: Coincident(g1,g2)
    c: Coincident(g2,g3)
    c: Coincident(g3,g0)
    c: Horizontal(g2)
    c: Vertical(g1)
    c: DistanceX(g0,g0) = 4.7625
    c: Symmetric(g2,g0,g-1)
    c: Symmetric(g0,g0,g-2)
    c: DistanceY(g3,g3) = 6
FEATURE [PartDesign::Pad] Pad010  label="LockingPinBodyPad"
  Direction = (1,1,1)
  Length = 59.9718
  Length2 = 100
  Midplane = true
  Placement = pos=(0,0,0) rot=(0.57735,0.57735,0.57735;2.0944rad)
  Profile = -> Sketch017
  Type = 0
  expr: Length = Sketch010.Constraints.DistanceFromCenterlineToOutsideOfBarInsertArm * 2 - <<TelescopingBarSettings>>.BarThickness * 3 - <<ProjectSettings>>.LooseTolerance * 2
FEATURE [Sketcher::SketchObject] Sketch018  label="LockingPinHoleSketch"
  FullyConstrained = true
  MapMode = 5
  Placement = pos=(0,0,0) rot=(0.57735,0.57735,0.57735;2.0944rad)
  Support = -> [YZ_Plane]
  expr: Constraints[8] = <<ProjectSettings>>.LockingPinWidth + <<ProjectSettings>>.LooseTolerance * 2
  expr: Constraints[9] = <<P90Measurements>>.PadWidestWidthOuterShoulderDistanceFromReferencePoint + (<<TelescopingBarSettings>>.BarHeight - <<TelescopingBarSettings>>.LockingPinHeight) / 2
  expr: Constraints[10] = <<ProjectSettings>>.WallThickness
  expr: Constraints[11] = <<P90Measurements>>.PadWidestWidthOuterShoulderDistanceFromReferencePoint + <<TelescopingBarSettings>>.BarHeight + <<TelescopingBarSettings>>.LockingPinHeight + <<ProjectSettings>>.LooseTolerance * 2
  sketch-geometry (4):
    g0: LineSegment StartX=4 StartY=90.039 StartZ=0 EndX=9.3625 EndY=90.039 EndZ=0
    g1: LineSegment StartX=9.3625 StartY=90.039 StartZ=0 EndX=9.3625 EndY=74.089 EndZ=0
    g2: LineSegment StartX=9.3625 StartY=74.089 StartZ=0 EndX=4 EndY=74.089 EndZ=0
    g3: LineSegment StartX=4 StartY=74.089 StartZ=0 EndX=4 EndY=90.039 EndZ=0
  constraints (12):
    c: Coincident(g0,g1)
    c: Coincident(g1,g2)
    c: Coincident(g2,g3)
    c: Coincident(g3,g0)
    c: Horizontal(g0)
    c: Horizontal(g2)
    c: Vertical(g1)
    c: Vertical(g3)
    c: DistanceX(g0,g0) = 5.3625
    c: DistanceY(g-1,g2) = 74.089
    c: DistanceX(g-1,g2) = 4
    c: DistanceY(g-1,g0) = 90.039
FEATURE [PartDesign::Pocket] Pocket007  label="LockingPinHolePocket"
  BaseFeature = -> Mirrored001
  Length = 60.5718
  Length2 = 100
  Midplane = true
  Placement = pos=(0,0,0) rot=(1,0,0;1.5708rad)
  Profile = -> Sketch018
  Type = 0
  expr: Length = <<LockingPinBodyPad>>.Length + <<ProjectSettings>>.LooseTolerance * 2
FEATURE [Sketcher::SketchObject] Sketch019  label="LockingButtonHoleSketch"
  FullyConstrained = true
  MapMode = 5
  Support = -> [XY_Plane]
  expr: Constraints[18] = <<ProjectSettings>>.WallThickness
  expr: Constraints[16] = <<ProjectSettings>>.LockingButtonHeight + <<ProjectSettings>>.LooseTolerance * 2
  expr: Constraints[17] = <<ProjectSettings>>.LockingButtonWidth + <<ProjectSettings>>.LooseTolerance * 2
  expr: Constraints[14] = <<ProjectSettings>>.StandardFillet
  sketch-geometry (8):
    g0: LineSegment StartX=-3.3 StartY=14.6 StartZ=0 EndX=3.3 EndY=14.6 EndZ=0
    g1: LineSegment StartX=5.3 StartY=12.6 StartZ=0 EndX=5.3 EndY=6 EndZ=0
    g2: LineSegment StartX=3.3 StartY=4 StartZ=0 EndX=-3.3 EndY=4 EndZ=0
    g3: LineSegment StartX=-5.3 StartY=6 StartZ=0 EndX=-5.3 EndY=12.6 EndZ=0
    g4: ArcOfCircle CenterX=-3.3 CenterY=12.6 CenterZ=0 NormalX=0 NormalY=0 NormalZ=1 AngleXU=0 Radius=2 StartAngle=1.5708 EndAngle=3.14159
    g5: ArcOfCircle CenterX=3.3 CenterY=12.6 CenterZ=0 NormalX=0 NormalY=0 NormalZ=1 AngleXU=0 Radius=2 StartAngle=0 EndAngle=1.5708
    g6: ArcOfCircle CenterX=3.3 CenterY=6 CenterZ=0 NormalX=0 NormalY=0 NormalZ=1 AngleXU=0 Radius=2 StartAngle=4.71239 EndAngle=6.28319
    g7: ArcOfCircle CenterX=-3.3 CenterY=6 CenterZ=0 NormalX=0 NormalY=0 NormalZ=1 AngleXU=0 Radius=2 StartAngle=3.14159 EndAngle=4.71239
  constraints (19):
    c: Horizontal(g2)
    c: Vertical(g1)
    c: Vertical(g3)
    c: Tangent(g3,g4) = 1.5708
    c: Tangent(g0,g4) = 1.5708
    c: Tangent(g0,g5) = 1.5708
    c: Tangent(g1,g5) = 1.5708
    c: Tangent(g2,g6) = 1.5708
    c: Tangent(g1,g6) = 1.5708
    c: Tangent(g2,g7) = 1.5708
    c: Tangent(g3,g7) = 1.5708
    c: Equal(g7,g4)
    c: Equal(g4,g5)
    c: Equal(g5,g6)
    c: Radius(g5) = 2
    c: Symmetric(g0,g0,g-2)
    c: DistanceY(g2,g0) = 10.6
    c: DistanceX(g3,g1) = 10.6
    c: DistanceY(g-1,g2) = 4
FEATURE [PartDesign::Pocket] Pocket008  label="LockingButtonHolePocket"
  BaseFeature = -> Pocket007
  Length = 116.414
  Length2 = 100
  Placement = pos=(0,0,0) rot=(1,0,0;1.5708rad)
  Profile = -> Sketch019
  Reversed = true
  Type = 0
  expr: Length = <<CentralPadSettings>>.LockingButtonHoleDepth + <<ProjectSettings>>.LockingButtonHoleClearanceForChamfer
FEATURE [Sketcher::SketchObject] Sketch020  label="ButtonBodySketch"
  AttachmentOffset = pos=(0,0,2) rot=(0,0,1;0rad)
  FullyConstrained = true
  MapMode = 5
  Placement = pos=(0,0,2) rot=(0,0,1;0rad)
  Support = -> [XY_Plane006]
  expr: Constraints[10] = <<ProjectSettings>>.StandardFillet
  expr: Constraints[16] = <<ProjectSettings>>.LockingButtonWidth - <<ProjectSettings>>.LooseTolerance * 2
  expr: Constraints[17] = <<ProjectSettings>>.LockingButtonWidth - <<ProjectSettings>>.LooseTolerance * 2
  sketch-geometry (8):
    g0: LineSegment StartX=-2.7 StartY=4.7 StartZ=0 EndX=2.7 EndY=4.7 EndZ=0
    g1: LineSegment StartX=4.7 StartY=2.7 StartZ=0 EndX=4.7 EndY=-2.7 EndZ=0
    g2: LineSegment StartX=2.7 StartY=-4.7 StartZ=0 EndX=-2.7 EndY=-4.7 EndZ=0
    g3: LineSegment StartX=-4.7 StartY=-2.7 StartZ=0 EndX=-4.7 EndY=2.7 EndZ=0
    g4: ArcOfCircle CenterX=-2.7 CenterY=2.7 CenterZ=0 NormalX=0 NormalY=0 NormalZ=1 AngleXU=0 Radius=2 StartAngle=1.5708 EndAngle=3.14159
    g5: ArcOfCircle CenterX=2.7 CenterY=2.7 CenterZ=0 NormalX=0 NormalY=0 NormalZ=1 AngleXU=0 Radius=2 StartAngle=0 EndAngle=1.5708
    g6: ArcOfCircle CenterX=2.7 CenterY=-2.7 CenterZ=0 NormalX=0 NormalY=0 NormalZ=1 AngleXU=0 Radius=2 StartAngle=4.71239 EndAngle=6.28319
    g7: ArcOfCircle CenterX=-2.7 CenterY=-2.7 CenterZ=0 NormalX=0 NormalY=0 NormalZ=1 AngleXU=0 Radius=2 StartAngle=3.14159 EndAngle=4.71239
  constraints (18):
    c: Horizontal(g0)
    c: Vertical(g1)
    c: Tangent(g3,g4) = 1.5708
    c: Tangent(g0,g4) = 1.5708
    c: Tangent(g1,g5) = 1.5708
    c: Tangent(g0,g5) = 1.5708
    c: Tangent(g1,g6) = 1.5708
    c: Tangent(g2,g6) = 1.5708
    c: Tangent(g2,g7) = 1.5708
    c: Tangent(g3,g7) = 1.5708
    c: Radius(g4) = 2
    c: Equal(g4,g5)
    c: Equal(g4,g6)
    c: Equal(g4,g7)
    c: Symmetric(g2,g2,g-2)
    c: Symmetric(g3,g3,g-1)
    c: DistanceX(g3,g1) = 9.4
    c: DistanceY(g2,g0) = 9.4
FEATURE [PartDesign::Pad] Pad011  label="ButtonBodyPad"
  Direction = (1,1,1)
  Length = 93.5015
  Length2 = 10
  Profile = -> Sketch020
  Type = 4
  expr: Length2 = <<ProjectSettings>>.LockingButtonActuationDistance + 4mm
  expr: Length = <<ProjectSettings>>.LockingButtonHoleDepth - <<ProjectSettings>>.SpringMaxHeight
FEATURE [Sketcher::SketchObject] Sketch021  label="ButtonLockingPinHoleSketch"
  FullyConstrained = true
  MapMode = 5
  Placement = pos=(0,0,0) rot=(0.57735,0.57735,0.57735;2.0944rad)
  Support = -> [YZ_Plane006]
  expr: Constraints[11] = <<ProjectSettings>>.LockingPinHeight + <<ProjectSettings>>.TightTolerance * 2
  expr: Constraints[9] = <<ProjectSettings>>.LockingButtonWidth / 2 + <<ProjectSettings>>.LooseTolerance
  expr: Constraints[7] = <<ProjectSettings>>.LockingPinWidth + <<ProjectSettings>>.TightTolerance * 2
  expr: Constraints[8] = <<P90Measurements>>.PadWidestWidthOuterShoulderDistanceFromReferencePoint + <<ProjectSettings>>.BarHeight / 2
  sketch-geometry (4):
    g0: LineSegment StartX=-5.3 StartY=83.289 StartZ=0 EndX=-0.3375 EndY=83.289 EndZ=0
    g1: LineSegment StartX=-0.3375 StartY=83.289 StartZ=0 EndX=-0.3375 EndY=77.089 EndZ=0
    g2: LineSegment StartX=-0.3375 StartY=77.089 StartZ=0 EndX=-5.3 EndY=77.089 EndZ=0
    g3: LineSegment StartX=-5.3 StartY=77.089 StartZ=0 EndX=-5.3 EndY=83.289 EndZ=0
  constraints (12):
    c: Coincident(g0,g1)
    c: Coincident(g1,g2)
    c: Coincident(g2,g3)
    c: Coincident(g3,g0)
    c: Horizontal(g2)
    c: Vertical(g1)
    c: Vertical(g3)
    c: DistanceX(g0,g0) = 4.9625
    c: DistanceY(g-1,g2) = 77.089
    c: DistanceX(g2,g-1) = 5.3
    c: Horizontal(g0)
    c: DistanceY(g3,g3) = 6.2
FEATURE [PartDesign::Pocket] Pocket009  label="ButtonLockingPinHolePocket"
  BaseFeature = -> Pad011
  Length = 5
  Length2 = 100
  Midplane = true
  Profile = -> Sketch021
  Type = 1
FEATURE [Sketcher::SketchObject] Sketch022  label="BCGHoleSketch"
  AttachmentOffset = pos=(0,0,4.8768) rot=(0,0,1;0rad)
  FullyConstrained = true
  MapMode = 5
  Placement = pos=(0,-4.8768,-1.1e-15) rot=(1,0,0;1.5708rad)
  Support = -> [XZ_Plane]
  expr: Constraints[1] = <<P90Measurements>>.PadBCGHoleFromReferencePoint + <<P90Measurements>>.PadBCGHoleDiameter / 2
  expr: Constraints[2] = <<P90Measurements>>.PadBCGHoleDiameter + <<ProjectSettings>>.LooseTolerance * 2
  expr: .AttachmentOffset.Base.z = <<P90Measurements>>.DovetailHeight
  sketch-geometry (1):
    g0: Circle CenterX=0 CenterY=79.6417 CenterZ=0 NormalX=0 NormalY=0 NormalZ=1 AngleXU=0 Radius=3.8179
  constraints (3):
    c: PointOnObject(g0,g-2)
    c: DistanceY(g-1,g0) = 79.6417
    c: Diameter(g0) = 7.6358
FEATURE [PartDesign::Pocket] Pocket010  label="BCGHolePocket"
  BaseFeature = -> Pocket008
  Length = 10.52
  Length2 = 100
  Placement = pos=(0,0,0) rot=(1,0,0;1.5708rad)
  Profile = -> Sketch022
  Refine = true
  Type = 0
FEATURE [Sketcher::SketchObject] Sketch024  label="BarCrosspinHoleSketch001"
  FullyConstrained = true
  MapMode = 5
  Placement = pos=(0,0,0) rot=(0.57735,0.57735,0.57735;2.0944rad)
  Support = -> [YZ_Plane007]
  expr: Constraints[2] = <<ProjectSettings>>.WallThickness + <<ProjectSettings>>.CrosspinWidth / 2 + <<ProjectSettings>>.TightTolerance
  expr: Constraints[1] = <<ProjectSettings>>.CrosspinWidth
  sketch-geometry (1):
    g0: Circle CenterX=-6.1 CenterY=0 CenterZ=0 NormalX=0 NormalY=0 NormalZ=1 AngleXU=0 Radius=2
  constraints (3):
    c: PointOnObject(g0,g-1)
    c: Diameter(g0) = 4
    c: DistanceX(g0,g-1) = 6.1
FEATURE [Sketcher::SketchObject] Sketch025  label="MainBarSketch001"
  FullyConstrained = true
  MapMode = 5
  Placement = pos=(0,0,0) rot=(1,0,0;1.5708rad)
  Support = -> [XZ_Plane007]
  expr: Constraints[9] = <<ProjectSettings>>.BarHeight
  expr: Constraints[8] = <<ProjectSettings>>.BarThickness
  sketch-geometry (4):
    g0: LineSegment StartX=-2.38125 StartY=6.35 StartZ=0 EndX=2.38125 EndY=6.35 EndZ=0
    g1: LineSegment StartX=2.38125 StartY=6.35 StartZ=0 EndX=2.38125 EndY=-6.35 EndZ=0
    g2: LineSegment StartX=2.38125 StartY=-6.35 StartZ=0 EndX=-2.38125 EndY=-6.35 EndZ=0
    g3: LineSegment StartX=-2.38125 StartY=-6.35 StartZ=0 EndX=-2.38125 EndY=6.35 EndZ=0
  constraints (10):
    c: Coincident(g0,g1)
    c: Coincident(g1,g2)
    c: Coincident(g2,g3)
    c: Coincident(g3,g0)
    c: Horizontal(g2)
    c: Vertical(g3)
    c: Symmetric(g1,g0,g-1)
    c: Symmetric(g0,g0,g-2)
    c: DistanceX(g0,g0) = 4.7625
    c: DistanceY(g3,g3) = 12.7
FEATURE [PartDesign::Pad] Pad013  label="MainBarPad001"
  Direction = (1,1,1)
  Length = 275
  Length2 = 100
  Placement = pos=(0,0,0) rot=(1,0,0;1.5708rad)
  Profile = -> Sketch025
  Type = 0
  expr: Length = <<ProjectSettings>>.BarLength
FEATURE [PartDesign::Pocket] Pocket011  label="BarCrosspinHolePocket001"
  BaseFeature = -> Pad013
  Length = 5
  Length2 = 100
  Midplane = true
  Placement = pos=(0,0,0) rot=(1,0,0;1.5708rad)
  Profile = -> Sketch024
  Type = 1
FEATURE [Sketcher::SketchObject] Sketch027  label="BarRackSketch001"
  FullyConstrained = true
  MapMode = 5
  Placement = pos=(0,0,0) rot=(0.57735,0.57735,0.57735;2.0944rad)
  Support = -> [YZ_Plane007]
  expr: Constraints[7] = <<ProjectSettings>>.LockingPinWidth + <<ProjectSettings>>.TightTolerance * 2
  expr: Constraints[9] = <<ProjectSettings>>.BarHeight / 2
  expr: Constraints[10] = <<ProjectSettings>>.LockingPinHeight + <<ProjectSettings>>.TightTolerance
  expr: Constraints[11] = <<ProjectSettings>>.WallThickness * 3 + <<ProjectSettings>>.CrosspinWidth + <<ProjectSettings>>.LockingButtonWidth
  sketch-geometry (4):
    g0: LineSegment StartX=-36.5655 StartY=-6.35 StartZ=0 EndX=-21.0375 EndY=-6.35 EndZ=0
    g1: LineSegment StartX=-21.0375 StartY=-6.35 StartZ=0 EndX=-21.0375 EndY=-0.25 EndZ=0
    g2: LineSegment StartX=-21.0375 StartY=-0.25 StartZ=0 EndX=-26 EndY=-0.25 EndZ=0
    g3: LineSegment StartX=-26 StartY=-0.25 StartZ=0 EndX=-36.5655 EndY=-6.35 EndZ=0
  constraints (12):
    c: Coincident(g0,g1)
    c: Coincident(g1,g2)
    c: Coincident(g2,g3)
    c: Coincident(g3,g0)
    c: Horizontal(g0)
    c: Horizontal(g2)
    c: Vertical(g1)
    c: DistanceX(g2,g2) = 4.9625
    c: Angle(g3,g2) = 2.61799
    c: DistanceY(g0,g-1) = 6.35
    c: DistanceY(g1,g1) = 6.1
    c: DistanceX(g2,g-1) = 26
FEATURE [PartDesign::Pocket] Pocket013  label="BarRackPocket001"
  BaseFeature = -> Pocket011
  Length = 5
  Length2 = 100
  Midplane = true
  Placement = pos=(0,0,0) rot=(1,0,0;1.5708rad)
  Profile = -> Sketch027
  Type = 1
FEATURE [Sketcher::SketchObject] Sketch028  label="FinalSlotSketch001"
  FullyConstrained = true
  MapMode = 5
  Placement = pos=(0,0,0) rot=(0.57735,0.57735,0.57735;2.0944rad)
  Support = -> [YZ_Plane007]
  expr: Constraints[9] = -1 * <<TelescopingBarSettings>>.BarHeight / 2
  expr: Constraints[8] = <<ProjectSettings>>.LockingPinWidth + <<ProjectSettings>>.LooseTolerance * 2
  expr: Constraints[10] = <<TelescopingBarSettings>>.LockingPinHeight
  expr: Constraints[11] = <<ProjectSettings>>.BarLength - <<ProjectSettings>>.EndcapSectionOnBarLength - <<ProjectSettings>>.WallThickness
  sketch-geometry (4):
    g0: LineSegment StartX=-250.637 StartY=-6.35 StartZ=0 EndX=-256 EndY=-6.35 EndZ=0
    g1: LineSegment StartX=-256 StartY=-6.35 StartZ=0 EndX=-256 EndY=-0.35 EndZ=0
    g2: LineSegment StartX=-256 StartY=-0.35 StartZ=0 EndX=-250.637 EndY=-0.35 EndZ=0
    g3: LineSegment StartX=-250.637 StartY=-0.35 StartZ=0 EndX=-250.637 EndY=-6.35 EndZ=0
  constraints (12):
    c: Coincident(g0,g1)
    c: Coincident(g1,g2)
    c: Coincident(g2,g3)
    c: Coincident(g3,g0)
    c: Horizontal(g0)
    c: Horizontal(g2)
    c: Vertical(g1)
    c: Vertical(g3)
    c: DistanceX(g2,g2) = 5.3625
    c: DistanceY(g-1,g0) = -6.35
    c: DistanceY(g3,g3) = 6
    c: DistanceX(g1,g-1) = 256
FEATURE [PartDesign::LinearPattern] LinearPattern001  label="BarRackPattern001"
  BaseFeature = -> Pocket013
  Direction = -> Sketch027 [H_Axis]
  Length = 198
  Occurrences = 6
  Originals = -> [Pocket013]
  Placement = pos=(0,0,0) rot=(1,0,0;1.5708rad)
  Reversed = true
  expr: Occurrences = <<TelescopingBarSettings>>.BarNumberOfKnotches
  expr: Length = (<<TelescopingBarSettings>>.BarLength - <<TelescopingBarSettings>>.BarOffsetFromCenter) / (Occurrences + 1) * Occurrences
FEATURE [PartDesign::Pocket] Pocket012  label="FinalSlotPad001"
  BaseFeature = -> LinearPattern001
  Length = 5
  Length2 = 100
  Midplane = true
  Placement = pos=(0,0,0) rot=(1,0,0;1.5708rad)
  Profile = -> Sketch028
  Refine = true
  Type = 1
FEATURE [PartDesign::Fillet] Fillet004  label="Slide Fillet"
  Base = -> Pad010 [Edge8]
  BaseFeature = -> Pad010
  Placement = pos=(0,0,0) rot=(0.57735,0.57735,0.57735;2.0944rad)
  Radius = 1
  SupportTransform = false
FEATURE [PartDesign::Body] Body004  label="LockingPin"
  Group = -> [Sketch017,Pad010,Fillet004]
  Origin = -> Origin005
  Placement = pos=(0,6.48125,80.139) rot=(0,0,1;0rad)
  Tip = -> Fillet004
  expr: .Placement.Base.y = <<ProjectSettings>>.WallThickness + <<ProjectSettings>>.LockingPinWidth / 2 + <<ProjectSettings>>.TightTolerance
  expr: .Placement.Base.z = <<P90Measurements>>.PadWidestWidthOuterShoulderDistanceFromReferencePoint + <<TelescopingBarSettings>>.BarHeight - <<TelescopingBarSettings>>.LockingPinHeight / 2 - <<ProjectSettings>>.LooseTolerance
FEATURE [Sketcher::SketchObject] Sketch029  label="LightningCutSketch"
  FullyConstrained = true
  MapMode = 5
  Placement = pos=(0,0,0) rot=(1,0,0;1.5708rad)
  Support = -> [XZ_Plane002]
  expr: Constraints[2] = <<P90Measurements>>.PadWidestWidth - <<ProjectSettings>>.TelescopingPadComfortFilletRadius * 3
  expr: Constraints[5] = <<P90Measurements>>.ButtOverallHeight - <<ProjectSettings>>.WallThickness * 2
  expr: Constraints[11] = <<ProjectSettings>>.WallThickness * 2
  sketch-geometry (6):
    g0: ArcOfCircle CenterX=-1.1391e-12 CenterY=26.1159 CenterZ=0 NormalX=0 NormalY=0 NormalZ=1 AngleXU=0 Radius=18.1159 StartAngle=3.14159 EndAngle=4.71239
    g1: LineSegment StartX=18.1159 StartY=26.1159 StartZ=0 EndX=18.1159 EndY=94.1023 EndZ=0
    g2: LineSegment StartX=-18.1159 StartY=26.1159 StartZ=0 EndX=-18.1159 EndY=94.1023 EndZ=0
    g3: ArcOfCircle CenterX=-6.2e-15 CenterY=94.1023 CenterZ=0 NormalX=0 NormalY=0 NormalZ=1 AngleXU=0 Radius=18.1159 StartAngle=1.5708 EndAngle=3.14159
    g4: ArcOfCircle CenterX=-6.2e-15 CenterY=94.1023 CenterZ=0 NormalX=0 NormalY=0 NormalZ=1 AngleXU=0 Radius=18.1159 StartAngle=0 EndAngle=1.5708
    g5: ArcOfCircle CenterX=2.401e-13 CenterY=26.1159 CenterZ=0 NormalX=0 NormalY=0 NormalZ=1 AngleXU=0 Radius=18.1159 StartAngle=4.71239 EndAngle=6.28319
  constraints (15):
    c: Vertical(g2)
    c: Vertical(g1)
    c: DistanceX(g2,g1) = 36.2318
    c: Tangent(g2,g3) = 1.5708
    c: Tangent(g1,g4) = -1.5708
    c: DistanceY(g-1,g3) = 112.218
    c: Tangent(g4,g3) = -1.5708
    c: PointOnObject(g3,g-2)
    c: Symmetric(g2,g1,g-2)
    c: Tangent(g1,g5) = -1.5708
    c: Tangent(g0,g2) = 1.5708
    c: DistanceY(g-1,g5) = 8
    c: Tangent(g0,g5) = -1.5708
    c: PointOnObject(g0,g-2)
    c: Horizontal(g0,g1)
FEATURE [PartDesign::Pocket] Pocket014  label="LightningCutPocket"
  BaseFeature = -> Fillet
  Length = 12
  Length2 = 100
  Placement = pos=(0,0,0) rot=(1,0,0;1.5708rad)
  Profile = -> Sketch029
  Type = 0
  expr: Length = <<ProjectSettings>>.TelescopingBarInsertDepth
FEATURE [Sketcher::SketchObject] Sketch030  label="ScrewEndHoleSketch"
  AttachmentOffset = pos=(0,0,-2.38125) rot=(0,0,1;0rad)
  FullyConstrained = true
  MapMode = 5
  Placement = pos=(-2.38125,5e-16,-5e-16) rot=(0.57735,0.57735,0.57735;2.0944rad)
  Support = -> [YZ_Plane007]
  expr: Constraints[2] = <<ProjectSettings>>.EndcapScrewBodyDiameter + <<ProjectSettings>>.LooseTolerance * 2
  expr: Constraints[1] = <<ProjectSettings>>.BarLength - <<ProjectSettings>>.EndcapSectionOnBarLength / 2
  expr: .AttachmentOffset.Base.z = -1 * <<ProjectSettings>>.BarThickness / 2
  sketch-geometry (1):
    g0: Circle CenterX=-267.5 CenterY=0 CenterZ=0 NormalX=0 NormalY=0 NormalZ=1 AngleXU=0 Radius=2.3
  constraints (3):
    c: PointOnObject(g0,g-1)
    c: DistanceX(g0,g-1) = 267.5
    c: Diameter(g0) = 4.6
FEATURE [Sketcher::SketchObject] Sketch031  label="InitialLFormSketch"
  FullyConstrained = true
  MapMode = 5
  Support = -> [XY_Plane010]
  expr: Constraints[17] = <<ProjectSettings>>.BarThickness
  expr: Constraints[18] = <<ProjectSettings>>.EndcapSectionOnBarLength - <<ProjectSettings>>.LooseTolerance
  expr: Constraints[19] = <<ProjectSettings>>.WallThickness
  sketch-geometry (7):
    g0: LineSegment StartX=0 StartY=14.7 StartZ=0 EndX=0 EndY=1.8e-15 EndZ=0
    g1: LineSegment StartX=0 StartY=1.8e-15 StartZ=0 EndX=4.7625 EndY=0 EndZ=0
    g2: LineSegment StartX=4.7625 StartY=0 StartZ=0 EndX=4.7625 EndY=-4 EndZ=0
    g3: LineSegment StartX=4.7625 StartY=-4 StartZ=0 EndX=-9e-16 EndY=-4 EndZ=0
    g4: LineSegment StartX=0 StartY=14.7 StartZ=0 EndX=-4 EndY=14.7 EndZ=0
    g5: LineSegment StartX=-4 StartY=14.7 StartZ=0 EndX=-4 EndY=1.8e-15 EndZ=0
    g6: ArcOfCircle CenterX=0 CenterY=1.8e-15 CenterZ=0 NormalX=0 NormalY=0 NormalZ=1 AngleXU=0 Radius=4 StartAngle=3.14159 EndAngle=4.71239
  constraints (20):
    c: PointOnObject(g0,g-2)
    c: Coincident(g0,g-1)
    c: Coincident(g0,g1)
    c: PointOnObject(g1,g-1)
    c: Coincident(g1,g2)
    c: Vertical(g2)
    c: Coincident(g2,g3)
    c: PointOnObject(g3,g-2)
    c: Horizontal(g3)
    c: Coincident(g0,g4)
    c: Coincident(g4,g5)
    c: Vertical(g5)
    c: Horizontal(g4)
    c: Horizontal(g5,g0)
    c: Coincident(g6,g0)
    c: Coincident(g6,g3)
    c: Coincident(g6,g5)
    c: DistanceX(g1,g1) = 4.7625
    c: DistanceY(g5,g5) = 14.7
    c: DistanceX(g4,g4) = 4
FEATURE [PartDesign::Pad] Pad014  label="InitialLFormPad"
  Direction = (1,1,1)
  Length = 12.7
  Length2 = 100
  Midplane = true
  Profile = -> Sketch031
  Type = 0
  expr: Length = <<TelescopingBarSettings>>.BarHeight
FEATURE [PartDesign::Fillet] Fillet012  label="Smoothing Fillet"
  Base = -> Pad014 [Edge19,Edge18]
  BaseFeature = -> Pad014
  Radius = 2
  SupportTransform = false
FEATURE [Sketcher::SketchObject] Sketch032  label="HexNutSketch"
  FullyConstrained = true
  MapMode = 5
  Placement = pos=(-4,0,0) rot=(0.57735,-0.57735,-0.57735;2.0944rad)
  Support = -> [Fillet012]
  expr: Constraints[18] = <<ProjectSettings>>.EndcapSectionOnBarLength / 2
  expr: Constraints[20] = <<TelescopingBarSettings>>.EndcapHexnutHeight + <<ProjectSettings>>.TightTolerance * 2
  sketch-geometry (7):
    g0: LineSegment StartX=-7.5 StartY=-4.11893 StartZ=0 EndX=-3.9329 EndY=-2.05947 EndZ=0
    g1: LineSegment StartX=-3.9329 StartY=-2.05947 StartZ=0 EndX=-3.9329 EndY=2.05947 EndZ=0
    g2: LineSegment StartX=-3.9329 StartY=2.05947 StartZ=0 EndX=-7.5 EndY=4.11893 EndZ=0
    g3: LineSegment StartX=-7.5 StartY=4.11893 StartZ=0 EndX=-11.0671 EndY=2.05947 EndZ=0
    g4: LineSegment StartX=-11.0671 StartY=2.05947 StartZ=0 EndX=-11.0671 EndY=-2.05947 EndZ=0
    g5: LineSegment StartX=-11.0671 StartY=-2.05947 StartZ=0 EndX=-7.5 EndY=-4.11893 EndZ=0
    g6: Circle CenterX=-7.5 CenterY=0 CenterZ=0 NormalX=0 NormalY=0 NormalZ=1 AngleXU=0 Radius=4.11893
  constraints (17):
    c: Coincident(g0,g1)
    c: Coincident(g1,g2)
    c: Coincident(g2,g3)
    c: Coincident(g3,g4)
    c: Coincident(g4,g5)
    c: Coincident(g5,g0)
    c: Equal(g0, g1-g5) x5
    c: PointOnObject(g0,g6)
    c: PointOnObject(g1,g6)
    c: PointOnObject(g2,g6)
    c: PointOnObject(g3,g6)
    c: PointOnObject(g4,g6)
    c: PointOnObject(g5,g6)
    c: PointOnObject(g6,g-1)
    c: DistanceX(g6,g-1) = 7.5
    c: Vertical(g0,g2)
    c: DistanceX(g3,g1) = 7.1342
FEATURE [PartDesign::Pocket] Pocket015  label="HexNutPocket"
  BaseFeature = -> Fillet012
  Length = 3.0734
  Length2 = 100
  Profile = -> Sketch032
  Type = 0
  expr: Length = <<TelescopingBarSettings>>.EndcapHexnutThickness
FEATURE [Sketcher::SketchObject] Sketch039  label="TelescopingPadLightningCutSketch"
  FullyConstrained = false
  MapMode = 5
  Placement = pos=(0,0,0) rot=(1,0,0;1.5708rad)
  Support = -> [Pocket010]
  sketch-geometry (16):
    g0: LineSegment StartX=-8.0398 StartY=-4.974 StartZ=0 EndX=-8.0398 EndY=-69.9702 EndZ=0
    g1: LineSegment StartX=-8.0398 StartY=-69.9702 StartZ=0 EndX=-17.2256 EndY=-69.9702 EndZ=0
    g2: LineSegment StartX=-17.2256 StartY=-69.9702 StartZ=0 EndX=-17.2256 EndY=-17.4923 EndZ=0
    g3: LineSegment StartX=17.2256 StartY=-17.4923 StartZ=0 EndX=17.2256 EndY=-69.9702 EndZ=0
    g4: LineSegment StartX=17.2256 StartY=-69.9702 StartZ=0 EndX=8.0398 EndY=-69.9702 EndZ=0
    g5: LineSegment StartX=8.0398 StartY=-69.9702 StartZ=0 EndX=8.0398 EndY=-4.974 EndZ=0
    g6: ArcOfCircle CenterX=-4.10281 CenterY=-17.4923 CenterZ=0 NormalX=0 NormalY=0 NormalZ=1 AngleXU=0 Radius=13.1228 StartAngle=1.8755 EndAngle=3.14159
    g7: ArcOfCircle CenterX=4.10281 CenterY=-17.4923 CenterZ=0 NormalX=0 NormalY=0 NormalZ=1 AngleXU=0 Radius=13.1228 StartAngle=0 EndAngle=1.26609
    g8: LineSegment StartX=-19.0379 StartY=-93.9856 StartZ=0 EndX=-8.0398 EndY=-93.9856 EndZ=0
    g9: LineSegment StartX=-8.0398 StartY=-93.9856 StartZ=0 EndX=-8.0398 EndY=-111.786 EndZ=0
    g10: LineSegment StartX=-19.0379 StartY=-100.932 StartZ=0 EndX=-19.0379 EndY=-93.9856 EndZ=0
    g11: LineSegment StartX=8.0398 StartY=-93.9856 StartZ=0 EndX=19.0379 EndY=-93.9856 EndZ=0
    g12: LineSegment StartX=19.0379 StartY=-93.9856 StartZ=0 EndX=19.0379 EndY=-100.932 EndZ=0
    g13: LineSegment StartX=8.0398 StartY=-111.786 StartZ=0 EndX=8.0398 EndY=-93.9856 EndZ=0
    g14: ArcOfCircle CenterX=0 CenterY=-92.6404 CenterZ=0 NormalX=0 NormalY=0 NormalZ=1 AngleXU=0 Radius=20.7651 StartAngle=3.55235 EndAngle=4.31482
    g15: ArcOfCircle CenterX=0 CenterY=-92.6404 CenterZ=0 NormalX=0 NormalY=0 NormalZ=1 AngleXU=0 Radius=20.7651 StartAngle=5.10996 EndAngle=5.87243
  constraints (39):
    c: Coincident(g0,g1)
    c: Coincident(g1,g2)
    c: Horizontal(g1)
    c: Vertical(g0)
    c: Vertical(g2)
    c: Coincident(g3,g4)
    c: Coincident(g4,g5)
    c: Horizontal(g4)
    c: Vertical(g3)
    c: Vertical(g5)
    c: Equal(g1,g4)
    c: Symmetric(g0,g4,g-2)
    c: Horizontal(g5,g0)
    c: Coincident(g6,g0)
    c: Coincident(g7,g5)
    c: Tangent(g7,g3) = 1.5708
    c: Horizontal(g2,g3)
    c: Tangent(g6,g2) = 1.5708
    c: Coincident(g8,g9)
    c: Coincident(g10,g8)
    c: Horizontal(g8)
    c: Vertical(g9)
    c: Vertical(g10)
    c: Coincident(g11,g12)
    c: Coincident(g13,g11)
    c: Horizontal(g11)
    c: Vertical(g12)
    c: Vertical(g13)
    c: Symmetric(g11,g8,g-2)
    c: Equal(g8,g11)
    c: Horizontal(g13,g9)
    c: Coincident(g14,g10)
    c: Coincident(g14,g9)
    c: Coincident(g15,g13)
    c: Coincident(g15,g12)
    c: Horizontal(g10,g12)
    c: PointOnObject(g15,g-2)
    c: PointOnObject(g14,g-2)
    c: Vertical(g8,g0)
FEATURE [PartDesign::Pocket] Pocket020  label="TelescopingPadLightningCutPocket"
  BaseFeature = -> Pocket010
  Length = 12
  Length2 = 100
  Placement = pos=(0,0,0) rot=(1,0,0;1.5708rad)
  Profile = -> Sketch039
  Type = 0
FEATURE [PartDesign::Fillet] Fillet016  label="BarHoleLargeFillet"
  Base = -> Pocket020 [Edge48,Edge74,Edge203,Edge186]
  BaseFeature = -> Pocket020
  Placement = pos=(0,0,0) rot=(1,0,0;1.5708rad)
  Radius = 3
  SupportTransform = false
FEATURE [PartDesign::Fillet] Fillet017  label="LockingBodytHardEdgeFillet"
  Base = -> Fillet016 [Edge91,Edge113,Edge152,Edge2]
  BaseFeature = -> Fillet016
  Placement = pos=(0,0,0) rot=(1,0,0;1.5708rad)
  Radius = 1
  SupportTransform = false
FEATURE [PartDesign::Fillet] Fillet018
  Base = -> Pocket009 [Face2]
  BaseFeature = -> Pocket009
  Radius = 2
  SupportTransform = false
FEATURE [PartDesign::Body] Body005  label="LockingButton"
  Group = -> [Sketch020,Pad011,Sketch021,Pocket009,Fillet018]
  Origin = -> Origin006
  Placement = pos=(0,9.3,0) rot=(0,0,1;0rad)
  Tip = -> Fillet018
  expr: .Placement.Base.y = <<ProjectSettings>>.LockingButtonHeight / 2 + <<ProjectSettings>>.WallThickness + <<ProjectSettings>>.LooseTolerance
FEATURE [App::Part] Part002  label="LockingMechanism"
  Group = -> [Body005,Body004]
  Origin = -> Origin009
  Placement = pos=(0,0,6.5) rot=(0,0,1;0rad)
FEATURE [PartDesign::Pocket] Pocket021
  BaseFeature = -> Pocket012
  Length = 5
  Length2 = 100
  Midplane = true
  Placement = pos=(0,0,0) rot=(1,0,0;1.5708rad)
  Profile = -> Sketch030
  Type = 1
FEATURE [PartDesign::Chamfer] Chamfer
  Angle = 45
  Base = -> Pocket021 [Edge36]
  BaseFeature = -> Pocket021
  ChamferType = 0
  FlipDirection = false
  Placement = pos=(0,0,0) rot=(1,0,0;1.5708rad)
  Size = 2.2606
  Size2 = 1
  SupportTransform = false
  expr: Size = <<ProjectSettings>>.ScrewCountersinkDepth
FEATURE [PartDesign::Body] Body006  label="RightTelescopingBar"
  Group = -> [Sketch025,Pad013,Sketch024,Pocket011,Sketch027,Pocket013,LinearPattern001,Sketch028,Pocket012,Sketch030,Pocket021,Chamfer]
  Origin = -> Origin007
  Placement = pos=(-27.9971,30,77.189) rot=(0,1,0;3.14159rad)
  Tip = -> Chamfer
  expr: .Placement.Base.z = <<P90Measurements>>.PadWidestWidthOuterShoulderDistanceFromReferencePoint + <<ProjectSettings>>.BarHeight / 2 + <<ProjectSettings>>.TightTolerance
  expr: .Placement.Base.x = -1 * (<<P90Measurements>>.PadWidestWidth / 2 + <<ProjectSettings>>.BarThickness / 2)
  expr: .Placement.Base.y = <<ProjectSettings>>.WallThickness * 4 + <<ProjectSettings>>.LockingButtonWidth + <<ProjectSettings>>.CrosspinWidth
FEATURE [Part::Mirroring] Part__Mirroring  label="LeftTelescopingBar"
  Base = (7.62939e-06,-109.238,77.289)
  Normal = (1,0,-1.19209e-07)
  Source = -> Body006
FEATURE [TechDraw::DrawSVGTemplate] Template
  EditableTexts = Designed_by_Name=Designed by Name; Drawing_number=Drawing number; FC-Date=Date; FC-SC=Scale; FC-SH=Sheet; FC-Title=Title; Subtitle=Subtitle; Weight=Weight
  Height = 210
  Orientation = 1
  Width = 297
FEATURE [Sketcher::SketchObject] Sketch040  label="HorizontalScallopSketch"
  FullyConstrained = true
  MapMode = 5
  Placement = pos=(0,0,0) rot=(0.57735,0.57735,0.57735;2.0944rad)
  Support = -> [YZ_Plane002]
  expr: Constraints[1] = <<ProjectSettings>>.ScallopRadius
  expr: Constraints[2] = <<TelescoptingPadBodyPad>>.Length
  sketch-geometry (5):
    g0: Circle CenterX=21 CenterY=0 CenterZ=0 NormalX=0 NormalY=0 NormalZ=1 AngleXU=0 Radius=1.5
    g1: LineSegment StartX=21 StartY=1.5 StartZ=0 EndX=19.5 EndY=0 EndZ=0
    g2: LineSegment StartX=19.5 StartY=0 StartZ=0 EndX=21 EndY=-1.5 EndZ=0
    g3: LineSegment StartX=21 StartY=-1.5 StartZ=0 EndX=22.5 EndY=0 EndZ=0
    g4: LineSegment StartX=22.5 StartY=0 StartZ=0 EndX=21 EndY=1.5 EndZ=0
  constraints (15):
    c: PointOnObject(g0,g-1)
    c: Radius(g0) = 1.5
    c: DistanceX(g-1,g0) = 21
    c: PointOnObject(g1,g0)
    c: PointOnObject(g1,g0)
    c: Coincident(g1,g2)
    c: PointOnObject(g2,g0)
    c: PointOnObject(g1,g-1)
    c: Coincident(g2,g3)
    c: PointOnObject(g3,g0)
    c: Coincident(g3,g4)
    c: Coincident(g4,g1)
    c: Vertical(g1,g0)
    c: Vertical(g0,g2)
    c: PointOnObject(g3,g-1)
FEATURE [PartDesign::Pocket] Pocket022  label="HorizontalScallopPocket"
  BaseFeature = -> Pocket014
  Length = 5
  Length2 = 100
  Midplane = true
  Placement = pos=(0,0,0) rot=(1,0,0;1.5708rad)
  Profile = -> Sketch040
  Type = 1
FEATURE [PartDesign::LinearPattern] LinearPattern  label="HorizontalScallopLinearPattern"
  BaseFeature = -> Pocket022
  Direction = -> Z_Axis002
  Length = 120.218
  Occurrences = 36
  Originals = -> [Pocket022]
  Placement = pos=(0,0,0) rot=(1,0,0;1.5708rad)
  expr: Occurrences = floor(Length / (<<ProjectSettings>>.ScallopRadius * 2 + <<ProjectSettings>>.DistanceBetweenScallops))
  expr: Length = <<P90Measurements>>.ButtOverallHeight
FEATURE [Sketcher::SketchObject] Sketch041  label="VerticalScallopSketch"
  FullyConstrained = true
  MapMode = 5
  Support = -> [XY_Plane002]
  expr: Constraints[0] = <<ProjectSettings>>.ScallopRadius
  expr: Constraints[1] = <<TelescoptingPadBodyPad>>.Length
  expr: Constraints[2] = <<P90Measurements>>.PadWidestWidth / 2 - <<ComfortFillet>>.Radius
  sketch-geometry (5):
    g0: Circle CenterX=-20.6159 CenterY=21 CenterZ=0 NormalX=0 NormalY=0 NormalZ=1 AngleXU=0 Radius=1.5
    g1: LineSegment StartX=-22.1159 StartY=21 StartZ=0 EndX=-20.6159 EndY=22.5 EndZ=0
    g2: LineSegment StartX=-20.6159 StartY=22.5 StartZ=0 EndX=-19.1159 EndY=21 EndZ=0
    g3: LineSegment StartX=-19.1159 StartY=21 StartZ=0 EndX=-20.6159 EndY=19.5 EndZ=0
    g4: LineSegment StartX=-20.6159 StartY=19.5 StartZ=0 EndX=-22.1159 EndY=21 EndZ=0
  constraints (15):
    c: Radius(g0) = 1.5
    c: DistanceY(g-1,g0) = 21
    c: DistanceX(g0,g-1) = 20.6159
    c: PointOnObject(g1,g0)
    c: PointOnObject(g1,g0)
    c: Coincident(g1,g2)
    c: PointOnObject(g2,g0)
    c: Coincident(g2,g3)
    c: PointOnObject(g3,g0)
    c: Coincident(g3,g4)
    c: Coincident(g4,g1)
    c: Vertical(g1,g0)
    c: Vertical(g3,g0)
    c: Horizontal(g1,g0)
    c: Horizontal(g2,g0)
FEATURE [PartDesign::Pocket] Pocket023  label="VerticalScallopPocket"
  BaseFeature = -> LinearPattern
  Length = 5
  Length2 = 100
  Midplane = true
  Placement = pos=(0,0,0) rot=(1,0,0;1.5708rad)
  Profile = -> Sketch041
  Type = 1
FEATURE [PartDesign::LinearPattern] LinearPattern002  label="VerticalScallopLinearPattern"
  BaseFeature = -> Pocket023
  Direction = -> X_Axis002
  Length = 41.2318
  Occurrences = 12
  Originals = -> [Pocket023]
  Placement = pos=(0,0,0) rot=(1,0,0;1.5708rad)
  Refine = true
  expr: Occurrences = floor(Length / (<<ProjectSettings>>.ScallopRadius * 2 + <<ProjectSettings>>.DistanceBetweenScallops))
  expr: Length = <<P90Measurements>>.PadWidestWidth - <<ComfortFillet>>.Radius * 2
FEATURE [PartDesign::Fillet] Fillet022  label="Comfort Fillet"
  Base = -> Fillet017 [Edge14,Edge12,Edge7,Edge9,Edge11,Edge13,Edge15,Edge17,Edge27,Edge18,Edge28,Edge30,Edge32,Edge34,Edge36,Edge38]
  BaseFeature = -> Fillet017
  Placement = pos=(0,0,0) rot=(1,0,0;1.5708rad)
  Radius = 1
  SupportTransform = false
FEATURE [PartDesign::Chamfer] Chamfer001  label="LockingPinInsertClearanceChamfer"
  Angle = 45
  Base = -> Fillet022 [Edge62,Edge230]
  BaseFeature = -> Fillet022
  ChamferType = 1
  FlipDirection = false
  Placement = pos=(0,0,0) rot=(1,0,0;1.5708rad)
  Size = 0.19
  Size2 = 6
  SupportTransform = false
FEATURE [TechDraw::DrawSVGTemplate] Template001
  EditableTexts = Designed_by_Name=Designed by Name; Drawing_number=Drawing number; FC-Date=Date; FC-SC=Scale; FC-SH=Sheet; FC-Title=Title; Subtitle=Subtitle; Weight=Weight
  Height = 210
  Orientation = 1
  Width = 297
FEATURE [TechDraw::DrawViewPart] View001
  CoarseView = false
  Direction = (0,1,0)
  Focus = 100
  HardHidden = false
  IsoCount = 0
  IsoHidden = false
  IsoVisible = false
  LockPosition = false
  Perspective = false
  Rotation = 0
  ScaleType = 0
  SeamHidden = false
  SeamVisible = true
  SmoothHidden = false
  SmoothVisible = true
  Source = -> [Body004]
  X = 148.135
  XDirection = (-1,0,0)
  Y = 107.922
FEATURE [TechDraw::DrawViewDimension] Dimension020
  Arbitrary = false
  ArbitraryTolerances = false
  EqualTolerance = true
  FormatSpec = %.2f
  FormatSpecOverTolerance = %+.2f
  FormatSpecUnderTolerance = %+.2f
  Inverted = false
  LockPosition = false
  MeasureType = 1
  OverTolerance = 0
  References2D = -> [View001]
  Rotation = 0
  ScaleType = 0
  TheoreticalExact = false
  Type = 1
  UnderTolerance = 0
  X = 1.09565
  Y = 24.1826
FEATURE [TechDraw::DrawViewDimension] Dimension021
  Arbitrary = false
  ArbitraryTolerances = false
  EqualTolerance = true
  FormatSpec = %.2f
  FormatSpecOverTolerance = %+.2f
  FormatSpecUnderTolerance = %+.2f
  Inverted = false
  LockPosition = false
  MeasureType = 1
  OverTolerance = 0
  References2D = -> [View001]
  Rotation = 0
  ScaleType = 0
  TheoreticalExact = false
  Type = 2
  UnderTolerance = 0
  X = -42.1381
  Y = -1.82609
FEATURE [TechDraw::DrawPage] Page001  label="LockingPinDrawing"
  KeepUpdated = true
  NextBalloonIndex = 1
  ProjectionType = 0
  Template = -> Template001
  Views = -> [View001,Dimension020,Dimension021]
FEATURE [PartDesign::Fillet] Fillet023  label="BarArmFillet"
  Base = -> LinearPattern002 [Edge306,Edge253,Edge665,Edge644,Edge4167,Edge3]
  BaseFeature = -> LinearPattern002
  Placement = pos=(0,0,0) rot=(1,0,0;1.5708rad)
  Radius = 2
  SupportTransform = false
  expr: Radius = <<ProjectSettings>>.StandardFillet
FEATURE [Sketcher::SketchObject] Sketch042  label="PaperworkLidNubSketch"
  AttachmentOffset = pos=(0,0,60.1091) rot=(0,0,1;0rad)
  FullyConstrained = true
  MapMode = 5
  Placement = pos=(0,0,60.1091) rot=(0,0,1;0rad)
  Support = -> [XY_Plane002]
  expr: Constraints[8] = (<<P90Measurements>>.PadWidestWidth - <<ProjectSettings>>.TelescopingPadComfortFilletRadius * 3) / 2
  expr: .AttachmentOffset.Base.z = <<P90Measurements>>.ButtOverallHeight / 2
  expr: Constraints[7] = <<LightningCutPocket>>.Length
  expr: Constraints[6] = <<ProjectSettings>>.PaperworkLidNubHeight + <<ProjectSettings>>.TightTolerance * 2
  expr: Constraints[5] = <<ProjectSettings>>.PaperworkLidNubWidth + <<ProjectSettings>>.TightTolerance * 2
  sketch-geometry (3):
    g0: LineSegment StartX=-18.1159 StartY=9.8 StartZ=0 EndX=-19.8159 EndY=10.9 EndZ=0
    g1: LineSegment StartX=-19.8159 StartY=10.9 StartZ=0 EndX=-18.1159 EndY=12 EndZ=0
    g2: LineSegment StartX=-18.1159 StartY=12 StartZ=0 EndX=-18.1159 EndY=9.8 EndZ=0
  constraints (9):
    c: Coincident(g0,g1)
    c: Coincident(g1,g2)
    c: Vertical(g2)
    c: Coincident(g2,g0)
    c: Equal(g1,g0)
    c: DistanceY(g2,g2) = 2.2
    c: DistanceX(g0,g0) = 1.7
    c: DistanceY(g-1,g1) = 12
    c: DistanceX(g1,g-1) = 18.1159
FEATURE [PartDesign::SubtractivePipe] SubtractivePipe  label="PaperworkLidNubSubtractivePipe"
  AuxilleryCurvelinear = true
  AuxillerySpineTangent = false
  BaseFeature = -> Fillet023
  Binormal = (0,0,0)
  Mode = 0
  Placement = pos=(0,0,0) rot=(1,0,0;1.5708rad)
  Profile = -> Sketch042
  Spine = -> Fillet023 [Edge305]
  SpineTangent = false
  Transformation = 0
  Transition = 0
FEATURE [PartDesign::Mirrored] Mirrored002  label="PaperworkLidNubSketchMirror"
  BaseFeature = -> SubtractivePipe
  MirrorPlane = -> Sketch042 [V_Axis]
  Originals = -> [SubtractivePipe]
  Placement = pos=(0,0,0) rot=(1,0,0;1.5708rad)
FEATURE [Sketcher::SketchObject] Sketch043  label="PaperworkLidMainSketch"
  FullyConstrained = true
  MapMode = 5
  Placement = pos=(0,0,0) rot=(1,0,0;1.5708rad)
  Support = -> [XZ_Plane011]
  expr: Constraints[11] = <<ProjectSettings>>.WallThickness * 2 + <<ProjectSettings>>.LooseTolerance
  expr: Constraints[5] = <<P90Measurements>>.ButtOverallHeight - <<ProjectSettings>>.WallThickness * 2 - <<ProjectSettings>>.LooseTolerance
  expr: Constraints[2] = <<P90Measurements>>.PadWidestWidth - <<ProjectSettings>>.TelescopingPadComfortFilletRadius * 3 - <<ProjectSettings>>.LooseTolerance * 2
  sketch-geometry (6):
    g0: ArcOfCircle CenterX=1e-15 CenterY=26.1159 CenterZ=0 NormalX=0 NormalY=0 NormalZ=1 AngleXU=0 Radius=17.8159 StartAngle=3.14159 EndAngle=4.71239
    g1: LineSegment StartX=17.8159 StartY=26.1159 StartZ=0 EndX=17.8159 EndY=94.1023 EndZ=0
    g2: LineSegment StartX=-17.8159 StartY=26.1159 StartZ=0 EndX=-17.8159 EndY=94.1023 EndZ=0
    g3: ArcOfCircle CenterX=-4.4e-15 CenterY=94.1023 CenterZ=0 NormalX=0 NormalY=0 NormalZ=1 AngleXU=0 Radius=17.8159 StartAngle=1.5708 EndAngle=3.14159
    g4: ArcOfCircle CenterX=-4.4e-15 CenterY=94.1023 CenterZ=0 NormalX=0 NormalY=0 NormalZ=1 AngleXU=0 Radius=17.8159 StartAngle=0 EndAngle=1.5708
    g5: ArcOfCircle CenterX=1e-15 CenterY=26.1159 CenterZ=0 NormalX=0 NormalY=0 NormalZ=1 AngleXU=0 Radius=17.8159 StartAngle=4.71239 EndAngle=6.28319
  constraints (15):
    c: Vertical(g2)
    c: Vertical(g1)
    c: DistanceX(g2,g1) = 35.6318
    c: Tangent(g2,g3) = 1.5708
    c: Tangent(g1,g4) = -1.5708
    c: DistanceY(g-1,g3) = 111.918
    c: Tangent(g4,g3) = -1.5708
    c: PointOnObject(g3,g-2)
    c: Symmetric(g2,g1,g-2)
    c: Tangent(g1,g5) = -1.5708
    c: Tangent(g0,g2) = 1.5708
    c: DistanceY(g-1,g5) = 8.3
    c: Tangent(g0,g5) = -1.5708
    c: PointOnObject(g0,g-2)
    c: Horizontal(g0,g1)
FEATURE [PartDesign::Pad] Pad015  label="PaperworkLidMainPad"
  Direction = (1,1,1)
  Length = 1.5
  Length2 = 100
  Placement = pos=(0,0,0) rot=(1,0,0;1.5708rad)
  Profile = -> Sketch043
  Reversed = true
  Type = 0
  expr: Length = <<ProjectSettings>>.PaperworklidbaseThickness
FEATURE [Sketcher::SketchObject] Sketch044  label="PaperworkLidWallAndNubSketch"
  AttachmentOffset = pos=(0,0,60.1091) rot=(0,0,1;0rad)
  FullyConstrained = true
  MapMode = 5
  Placement = pos=(0,0,60.1091) rot=(0,0,1;0rad)
  Support = -> [XY_Plane011]
  expr: Constraints[20] = <<ProjectSettings>>.PaperwokLipInteriorWallAngle
  expr: Constraints[19] = <<ProjectSettings>>.PaperworkLipTabWallFilletRadius
  expr: Constraints[17] = <<ProjectSettings>>.PaperworkLidWallThickness
  expr: Constraints[14] = <<ProjectSettings>>.PaperworklidbaseThickness
  expr: Constraints[9] = <<ProjectSettings>>.PaperworkLidNubHeight
  expr: .AttachmentOffset.Base.z = <<P90Measurements>>.ButtOverallHeight / 2
  expr: Constraints[6] = (<<P90Measurements>>.PadWidestWidth - <<ProjectSettings>>.TelescopingPadComfortFilletRadius * 3 - <<ProjectSettings>>.LooseTolerance * 2) / 2
  expr: Constraints[10] = <<LightningCutPocket>>.Length - <<ProjectSettings>>.LooseTolerance
  expr: Constraints[8] = <<ProjectSettings>>.PaperworkLidNubWidth
  sketch-geometry (7):
    g0: LineSegment StartX=-17.8159 StartY=0 StartZ=0 EndX=-17.8159 EndY=9.7 EndZ=0
    g1: LineSegment StartX=-17.8159 StartY=9.7 StartZ=0 EndX=-19.3159 EndY=10.7 EndZ=0
    g2: LineSegment StartX=-19.3159 StartY=10.7 StartZ=0 EndX=-17.8159 EndY=11.7 EndZ=0
    g3: LineSegment StartX=-17.8159 StartY=11.7 StartZ=0 EndX=-15.8159 EndY=11.7 EndZ=0
    g4: ArcOfCircle CenterX=-7.61753 CenterY=5.5 CenterZ=0 NormalX=0 NormalY=0 NormalZ=1 AngleXU=0 Radius=4 StartAngle=3.66519 EndAngle=4.71239
    g5: LineSegment StartX=-11.0816 StartY=3.5 StartZ=0 EndX=-15.8159 EndY=11.7 EndZ=0
    g6: LineSegment StartX=-17.8159 StartY=0 StartZ=0 EndX=-7.61753 EndY=1.5 EndZ=0
  constraints (21):
    c: PointOnObject(g0,g-1)
    c: Vertical(g0)
    c: Coincident(g0,g1)
    c: Coincident(g1,g2)
    c: Coincident(g2,g3)
    c: Horizontal(g3)
    c: DistanceX(g0,g-1) = 17.8159
    c: Equal(g1,g2)
    c: DistanceY(g0,g2) = 2
    c: DistanceX(g1,g0) = 1.5
    c: DistanceY(g-1,g3) = 11.7
    c: Vertical(g2,g0)
    c: Coincident(g5,g3)
    c: Tangent(g5,g4) = 1.5708
    c: DistanceY(g6,g4) = 1.5
    c: Vertical(g4,g4)
    c: Coincident(g6,g4)
    c: DistanceX(g3,g3) = 2
    c: Coincident(g6,g0)
    c: Radius(g4) = 4
    c: Angle(g3,g5) = 2.0944
FEATURE [PartDesign::AdditivePipe] AdditivePipe  label="PaperworkLidWallAndNubAdditivePipe"
  AuxilleryCurvelinear = true
  AuxillerySpineTangent = false
  BaseFeature = -> Pad015
  Binormal = (0,0,0)
  Mode = 0
  Placement = pos=(0,0,0) rot=(1,0,0;1.5708rad)
  Profile = -> Sketch044
  Spine = -> Pad015 [Edge17]
  SpineTangent = false
  Transformation = 0
  Transition = 0
FEATURE [PartDesign::Mirrored] Mirrored003  label="PaperworkLidWallAndNubMirrored"
  BaseFeature = -> AdditivePipe
  MirrorPlane = -> Sketch044 [V_Axis]
  Originals = -> [AdditivePipe]
  Placement = pos=(0,0,0) rot=(1,0,0;1.5708rad)
  Refine = true
FEATURE [Sketcher::SketchObject] Sketch045  label="PaperworkLidCrosspinSlotSketch"
  FullyConstrained = true
  MapMode = 5
  Placement = pos=(0,0,0) rot=(0.57735,0.57735,0.57735;2.0944rad)
  Support = -> [YZ_Plane011]
  expr: Constraints[8] = <<LightningCutPocket>>.Length
  expr: Constraints[2] = <<ProjectSettings>>.CrosspinWidth + <<ProjectSettings>>.LooseTolerance * 2
  expr: Constraints[1] = <<TelescopingPadSettings>>.TelescopingBarInsertDepth / 2 + <<ProjectSettings>>.TightTolerance * 2
  expr: Constraints[0] = <<P90Measurements>>.PadWidestWidthOuterShoulderDistanceFromReferencePoint + <<ProjectSettings>>.BarHeight / 2 + <<ProjectSettings>>.TightTolerance
  expr: Constraints[14] = <<ProjectSettings>>.StandardFillet
  sketch-geometry (10):
    g0: ArcOfCircle CenterX=5.8875 CenterY=77.189 CenterZ=0 NormalX=0 NormalY=0 NormalZ=1 AngleXU=0 Radius=2.3 StartAngle=1.5708 EndAngle=4.71239
    g1: LineSegment StartX=5.8875 StartY=79.489 StartZ=0 EndX=10 EndY=79.489 EndZ=0
    g2: LineSegment StartX=12 StartY=79.489 StartZ=0 EndX=12 EndY=74.889 EndZ=0
    g3: LineSegment StartX=10 StartY=74.889 StartZ=0 EndX=5.8875 EndY=74.889 EndZ=0
    g4: LineSegment StartX=12 StartY=79.489 StartZ=0 EndX=12 EndY=81.489 EndZ=0
    g5: ArcOfCircle CenterX=10 CenterY=81.489 CenterZ=0 NormalX=0 NormalY=0 NormalZ=1 AngleXU=0 Radius=2 StartAngle=4.71239 EndAngle=6.28319
    g6: GeomPoint X=12 Y=79.489 Z=0
    g7: LineSegment StartX=12 StartY=74.889 StartZ=0 EndX=12 EndY=72.889 EndZ=0
    g8: ArcOfCircle CenterX=10 CenterY=72.889 CenterZ=0 NormalX=0 NormalY=0 NormalZ=1 AngleXU=0 Radius=2 StartAngle=-2.7e-15 EndAngle=1.5708
    g9: GeomPoint X=12 Y=74.889 Z=0
  constraints (25):
    c: DistanceY(g-1,g0) = 77.189
    c: DistanceX(g-1,g0) = 5.8875
    c: Diameter(g0) = 4.6
    c: Coincident(g6,g2)
    c: Coincident(g2,g9)
    c: Horizontal(g1)
    c: Horizontal(g3)
    c: Vertical(g2)
    c: DistanceX(g-1,g6) = 12
    c: Vertical(g3,g0)
    c: Coincident(g0,g1)
    c: Coincident(g0,g3)
    c: Vertical(g0,g0)
    c: Vertical(g4)
    c: DistanceY(g6,g4) = 2
    c: PointOnObject(g6,g1)
    c: Tangent(g1,g5) = -1.5708
    c: Coincident(g4,g2)
    c: Tangent(g5,g4) = -1.5708
    c: Vertical(g7)
    c: PointOnObject(g9,g3)
    c: Tangent(g3,g8) = -1.5708
    c: Coincident(g7,g2)
    c: Tangent(g8,g7) = 1.5708
    c: Equal(g8,g5)
FEATURE [PartDesign::Pocket] Pocket024  label="PaperworkLidCrosspinSlotPocket"
  BaseFeature = -> Mirrored003
  Length = 5
  Length2 = 100
  Midplane = true
  Placement = pos=(0,0,0) rot=(1,0,0;1.5708rad)
  Profile = -> Sketch045
  Type = 1
FEATURE [Sketcher::SketchObject] Sketch046  label="PaperworkLidFingerHoleSketch"
  AttachmentOffset = pos=(0,0,60.1091) rot=(0,0,1;0rad)
  FullyConstrained = false
  MapMode = 5
  Placement = pos=(0,0,60.1091) rot=(0,0,1;0rad)
  Support = -> [XY_Plane011]
  expr: .AttachmentOffset.Base.z = <<P90Measurements>>.ButtOverallHeight / 2
  expr: Constraints[7] = <<ProjectSettings>>.PaperworkLidFingerHoleDiameter / 2
  expr: Constraints[6] = <<ProjectSettings>>.PaperworklidbaseThickness
  sketch-geometry (7):
    g0: LineSegment StartX=0 StartY=0 StartZ=0 EndX=10 EndY=0 EndZ=0
    g1: LineSegment StartX=10 StartY=1.5 StartZ=0 EndX=0 EndY=1.5 EndZ=0
    g2: LineSegment StartX=0 StartY=1.5 StartZ=0 EndX=0 EndY=0 EndZ=0
    g3: ArcOfCircle CenterX=10 CenterY=0.75 CenterZ=0 NormalX=0 NormalY=0 NormalZ=1 AngleXU=0 Radius=0.75 StartAngle=1.5708 EndAngle=4.71239
    g4: LineSegment StartX=0 StartY=1.5 StartZ=0 EndX=0 EndY=8.15565 EndZ=0
    g5: LineSegment StartX=0 StartY=8.15565 StartZ=0 EndX=10 EndY=8.15565 EndZ=0
    g6: LineSegment StartX=10 StartY=8.15565 StartZ=0 EndX=10 EndY=1.5 EndZ=0
  constraints (19):
    c: Coincident(g1,g2)
    c: Coincident(g2,g0)
    c: Horizontal(g0)
    c: Horizontal(g1)
    c: Vertical(g2)
    c: Coincident(g0,g-1)
    c: DistanceY(g2,g2) = 1.5
    c: DistanceX(g1,g1) = 10
    c: Coincident(g3,g1)
    c: Coincident(g3,g0)
    c: Vertical(g3,g0)
    c: Vertical(g0,g1)
    c: Coincident(g1,g4)
    c: PointOnObject(g4,g-2)
    c: Coincident(g4,g5)
    c: Horizontal(g5)
    c: Coincident(g5,g6)
    c: Vertical(g6)
    c: Coincident(g6,g1)
FEATURE [PartDesign::Groove] Groove  label="PaperworkLidFingerHoleGroove"
  Angle = 360
  Axis = (0,1,0)
  Base = (0,0,60.1091)
  BaseFeature = -> Pocket024
  Placement = pos=(0,0,0) rot=(1,0,0;1.5708rad)
  Profile = -> Sketch046
  ReferenceAxis = -> Sketch046 [V_Axis]
FEATURE [PartDesign::Body] Body008  label="PaperworkLid"
  Group = -> [Sketch043,Pad015,Sketch044,AdditivePipe,Mirrored003,Sketch045,Pocket024,Sketch046,Groove]
  Origin = -> Origin011
  Placement = pos=(0,18,0) rot=(0,0,1;0rad)
  Tip = -> Groove
  expr: .Placement.Base.y = <<PadBodyPad>>.Length
FEATURE [PartDesign::Fillet] Fillet024  label="interior fillet"
  Base = -> Mirrored002 [Edge128]
  BaseFeature = -> Mirrored002
  Placement = pos=(0,0,0) rot=(1,0,0;1.5708rad)
  Radius = 1
  SupportTransform = false
FEATURE [PartDesign::Chamfer] Chamfer002  label="crosspinholechamfer"
  Angle = 45
  Base = -> Fillet024 [Edge163,Edge134]
  BaseFeature = -> Fillet024
  ChamferType = 0
  FlipDirection = false
  Placement = pos=(0,0,0) rot=(1,0,0;1.5708rad)
  Size = 1.5
  Size2 = 1
  SupportTransform = false
FEATURE [PartDesign::Body] Body002  label="TelescopingPad"
  Group = -> [Sketch008,Pad006,Sketch009,Pocket002,Sketch010,Pad007,Sketch011,Mirrored,Pocket003,Fillet,Sketch029,Pocket014,Sketch040,Pocket022,LinearPattern,Sketch041,Pocket023,LinearPattern002,Fillet023,Sketch042,SubtractivePipe,Mirrored002,Fillet024,Chamfer002]
  Origin = -> Origin002
  Placement = pos=(0,18,0) rot=(0,0,1;0rad)
  Tip = -> Chamfer002
  expr: .Placement.Base.y = <<PadBodyPad>>.Length
FEATURE [PartDesign::Chamfer] Chamfer003  label="LockingButtonOverhangChamfer"
  Angle = 45
  Base = -> Chamfer001 [Face14]
  BaseFeature = -> Chamfer001
  ChamferType = 0
  FlipDirection = false
  Placement = pos=(0,0,0) rot=(1,0,0;1.5708rad)
  Size = 4.5
  Size2 = 1
  SupportTransform = false
  expr: Size = <<ProjectSettings>>.LockingButtonHoleClearanceForChamfer
FEATURE [Sketcher::SketchObject] Sketch047  label="MainTelescopingBodyLockingPinOverhangCompensationSketch"
  AttachmentOffset = pos=(0,0,-4) rot=(0,0,1;0rad)
  FullyConstrained = true
  MapMode = 5
  Placement = pos=(0,4,9e-16) rot=(1,0,0;1.5708rad)
  Support = -> [XZ_Plane]
  expr: Constraints[9] = Spreadsheet001.LockingPinPocketOverhangCompensationDistance + <<ProjectSettings>>.TightTolerance
  expr: Constraints[8] = 90deg - <<CentralPadTelescopingBarInsertArmSketch>>.Constraints.BarArmAngle
  expr: .AttachmentOffset.Base.z = -1 * <<ProjectSettings>>.WallThickness
  expr: Constraints[7] = <<P90Measurements>>.PadWidestWidthOuterShoulderDistanceFromReferencePoint + <<TelescopingBarSettings>>.BarHeight + <<TelescopingBarSettings>>.LockingPinHeight + <<ProjectSettings>>.LooseTolerance * 2
  expr: Constraints[4] = <<LockingPinHolePocket>>.Length
  sketch-geometry (4):
    g0: LineSegment StartX=-30.2859 StartY=90.039 StartZ=0 EndX=30.2859 EndY=90.039 EndZ=0
    g1: LineSegment StartX=30.2859 StartY=90.039 StartZ=0 EndX=29.1656 EndY=91.639 EndZ=0
    g2: LineSegment StartX=29.1656 StartY=91.639 StartZ=0 EndX=-29.1656 EndY=91.639 EndZ=0
    g3: LineSegment StartX=-29.1656 StartY=91.639 StartZ=0 EndX=-30.2859 EndY=90.039 EndZ=0
  constraints (10):
    c: Coincident(g0,g1)
    c: Coincident(g1,g2)
    c: Coincident(g2,g3)
    c: Coincident(g3,g0)
    c: DistanceX(g0,g0) = 60.5718
    c: Symmetric(g0,g0,g-2)
    c: Symmetric(g2,g1,g-2)
    c: DistanceY(g-1,g0) = 90.039
    c: Angle(g1,g0) = 0.959931
    c: DistanceY(g0,g1) = 1.6
FEATURE [PartDesign::Pocket] Pocket025  label="MainTelescopingBodyLockingPinOverhangCompensationPocket"
  BaseFeature = -> Chamfer003
  Length = 5.3625
  Length2 = 100
  Placement = pos=(0,0,0) rot=(1,0,0;1.5708rad)
  Profile = -> Sketch047
  Refine = true
  Type = 0
  expr: Length = <<ProjectSettings>>.LockingPinWidth + <<ProjectSettings>>.LooseTolerance * 2
FEATURE [PartDesign::Chamfer] Chamfer004  label="MainTelescopingBodyLockingPinOverhangCompensationChamfer"
  Angle = 45
  Base = -> Pocket025 [Edge64,Edge165,Edge167,Edge65]
  BaseFeature = -> Pocket025
  ChamferType = 0
  FlipDirection = false
  Placement = pos=(0,0,0) rot=(1,0,0;1.5708rad)
  Size = 2
  Size2 = 1
  SupportTransform = false
FEATURE [PartDesign::Body] Body  label="MainTelescopingBody"
  Group = -> [Sketch,Pad,Sketch001,Pad001,Sketch002,Pocket,Sketch003,Pad002,Sketch004,Pocket001,Sketch014,Pad008,Mirrored001,Sketch018,Pocket007,Sketch019,Pocket008,Sketch022,Pocket010,Sketch039,Pocket020,Fillet016,Fillet017,Fillet022,Chamfer001,Chamfer003,Sketch047,Pocket025,Chamfer004]
  Origin = -> Origin
  Tip = -> Chamfer004
FEATURE [App::Part] Part001  label="LockingAssembly"
  Group = -> [Body,Part002]
  Origin = -> Origin008
  Placement = pos=(0,205,0) rot=(0,0,1;0rad)
FEATURE [TechDraw::DrawViewPart] View
  CoarseView = false
  Direction = (-1,0,0)
  Focus = 100
  HardHidden = false
  IsoCount = 0
  IsoHidden = false
  IsoVisible = false
  LockPosition = false
  Perspective = false
  Rotation = 0
  ScaleType = 0
  SeamHidden = false
  SeamVisible = true
  SmoothHidden = false
  SmoothVisible = true
  Source = -> [Body006]
  X = 148.865
  XDirection = (0,-1,0)
  Y = 119.036
FEATURE [TechDraw::DrawViewDimension] Dimension016
  Arbitrary = false
  ArbitraryTolerances = false
  EqualTolerance = true
  FormatSpec = %.2f
  FormatSpecOverTolerance = %+.2f
  FormatSpecUnderTolerance = %+.2f
  Inverted = false
  LockPosition = false
  MeasureType = 1
  OverTolerance = 0
  References2D = -> [View]
  Rotation = 0
  ScaleType = 0
  TheoreticalExact = false
  Type = 2
  UnderTolerance = 0
  X = -125.015
  Y = 21.8438
FEATURE [TechDraw::DrawViewDimension] Dimension019
  Arbitrary = false
  ArbitraryTolerances = false
  EqualTolerance = true
  FormatSpec = %.2f
  FormatSpecOverTolerance = %+.2f
  FormatSpecUnderTolerance = %+.2f
  Inverted = false
  LockPosition = false
  MeasureType = 1
  OverTolerance = 0
  References2D = -> [View]
  Rotation = 0
  ScaleType = 0
  TheoreticalExact = false
  Type = 1
  UnderTolerance = 0
  X = -48.9457
  Y = 28.224
FEATURE [TechDraw::DrawViewDimension] Dimension017
  Arbitrary = false
  ArbitraryTolerances = false
  EqualTolerance = true
  FormatSpec = %.2f
  FormatSpecOverTolerance = %+.2f
  FormatSpecUnderTolerance = %+.2f
  Inverted = false
  LockPosition = false
  MeasureType = 1
  OverTolerance = 0
  References2D = -> [View]
  Rotation = 0
  ScaleType = 0
  TheoreticalExact = false
  Type = 2
  UnderTolerance = 0
  X = 103.787
  Y = 14.2875
FEATURE [TechDraw::DrawViewDimension] Dimension013
  Arbitrary = false
  ArbitraryTolerances = false
  EqualTolerance = true
  FormatSpec = %.2f
  FormatSpecOverTolerance = %+.2f
  FormatSpecUnderTolerance = %+.2f
  Inverted = false
  LockPosition = false
  MeasureType = 1
  OverTolerance = 0
  References2D = -> [View]
  Rotation = 0
  ScaleType = 0
  TheoreticalExact = false
  Type = 1
  UnderTolerance = 0
  X = 103.67
  Y = 24.2302
FEATURE [TechDraw::DrawViewDimension] Dimension010
  Arbitrary = false
  ArbitraryTolerances = false
  EqualTolerance = true
  FormatSpec = %.2f
  FormatSpecOverTolerance = %+.2f
  FormatSpecUnderTolerance = %+.2f
  Inverted = false
  LockPosition = false
  MeasureType = 1
  OverTolerance = 0
  References2D = -> [View]
  Rotation = 0
  ScaleType = 0
  TheoreticalExact = false
  Type = 1
  UnderTolerance = 0
  X = -126.518
  Y = 48.2771
FEATURE [TechDraw::DrawViewDimension] Dimension011
  Arbitrary = false
  ArbitraryTolerances = false
  EqualTolerance = true
  FormatSpec = %.2f
  FormatSpecOverTolerance = %+.2f
  FormatSpecUnderTolerance = %+.2f
  Inverted = false
  LockPosition = false
  MeasureType = 1
  OverTolerance = 0
  References2D = -> [View]
  Rotation = 0
  ScaleType = 0
  TheoreticalExact = false
  Type = 1
  UnderTolerance = 0
  X = 127.089
  Y = 30.2302
FEATURE [TechDraw::DrawViewDimension] Dimension012
  Arbitrary = false
  ArbitraryTolerances = false
  EqualTolerance = true
  FormatSpec = %.2f
  FormatSpecOverTolerance = %+.2f
  FormatSpecUnderTolerance = %+.2f
  Inverted = false
  LockPosition = false
  MeasureType = 1
  OverTolerance = 0
  References2D = -> [View]
  Rotation = 0
  ScaleType = 0
  TheoreticalExact = false
  Type = 1
  UnderTolerance = 0
  X = -108.496
  Y = 39.5271
FEATURE [TechDraw::DrawViewDimension] Dimension
  Arbitrary = false
  ArbitraryTolerances = false
  EqualTolerance = true
  FormatSpec = %.2f
  FormatSpecOverTolerance = %+.2f
  FormatSpecUnderTolerance = %+.2f
  Inverted = false
  LockPosition = false
  MeasureType = 1
  OverTolerance = 0
  References2D = -> [View]
  Rotation = 0
  ScaleType = 0
  TheoreticalExact = false
  Type = 1
  UnderTolerance = 0
  X = -0.546875
  Y = -22.7563
FEATURE [TechDraw::DrawViewDimension] Dimension014
  Arbitrary = false
  ArbitraryTolerances = false
  EqualTolerance = true
  FormatSpec = ⌀%.2f
  FormatSpecOverTolerance = %+.2f
  FormatSpecUnderTolerance = %+.2f
  Inverted = false
  LockPosition = false
  MeasureType = 1
  OverTolerance = 0
  References2D = -> [View]
  Rotation = 0
  ScaleType = 0
  TheoreticalExact = false
  Type = 5
  UnderTolerance = 0
  X = -125.964
  Y = -16.7708
FEATURE [TechDraw::DrawViewDimension] Dimension015
  Arbitrary = false
  ArbitraryTolerances = false
  EqualTolerance = true
  FormatSpec = ⌀%.2f
  FormatSpecOverTolerance = %+.2f
  FormatSpecUnderTolerance = %+.2f
  Inverted = false
  LockPosition = false
  MeasureType = 1
  OverTolerance = 0
  References2D = -> [View]
  Rotation = 0
  ScaleType = 0
  TheoreticalExact = false
  Type = 5
  UnderTolerance = 0
  X = 118.854
  Y = -15.6771
FEATURE [TechDraw::DrawViewDimension] Dimension018
  Arbitrary = false
  ArbitraryTolerances = false
  EqualTolerance = true
  FormatSpec = %.2f
  FormatSpecOverTolerance = %+.2f
  FormatSpecUnderTolerance = %+.2f
  Inverted = false
  LockPosition = false
  MeasureType = 1
  OverTolerance = 0
  References2D = -> [View]
  Rotation = 0
  ScaleType = 0
  TheoreticalExact = false
  Type = 1
  UnderTolerance = 0
  X = -60.3599
  Y = 37.8844
FEATURE [TechDraw::DrawPage] Page  label="TelescopingArmDrawing"
  KeepUpdated = true
  NextBalloonIndex = 2
  ProjectionType = 0
  Template = -> Template
  Views = -> [View,Dimension,Dimension010,Dimension011,Dimension012,Dimension013,Dimension014,Dimension015,Dimension016,Dimension017,Dimension018,Dimension019]
FEATURE [Sketcher::SketchObject] Sketch048  label="EndcapScrewBodyHoleSketch"
  FullyConstrained = true
  MapMode = 5
  Placement = pos=(0,0,0) rot=(0.57735,0.57735,0.57735;2.0944rad)
  Support = -> [YZ_Plane010]
  expr: Constraints[1] = <<ProjectSettings>>.EndcapSectionOnBarLength / 2
  expr: Constraints[2] = <<ProjectSettings>>.EndcapScrewBodyDiameter + <<ProjectSettings>>.LooseTolerance
  sketch-geometry (1):
    g0: Circle CenterX=7.5 CenterY=0 CenterZ=0 NormalX=0 NormalY=0 NormalZ=1 AngleXU=0 Radius=2.15
  constraints (3):
    c: PointOnObject(g0,g-1)
    c: DistanceX(g-1,g0) = 7.5
    c: Diameter(g0) = 4.3
FEATURE [PartDesign::Pocket] Pocket026  label="EndcapScrewBodyHolePocket"
  BaseFeature = -> Pocket015
  Length = 5
  Length2 = 100
  Profile = -> Sketch048
  Type = 1
FEATURE [PartDesign::Fillet] Fillet025  label="Minor Fillet"
  Base = -> Pocket026 [Edge34,Edge1]
  BaseFeature = -> Pocket026
  Radius = 1
  SupportTransform = false
FEATURE [PartDesign::Body] Body007  label="Endcap"
  Group = -> [Sketch031,Pad014,Fillet012,Sketch032,Pocket015,Sketch048,Pocket026,Fillet025]
  Origin = -> Origin010
  Placement = pos=(-30.3784,-245,77.189) rot=(0,0,1;0rad)
  Tip = -> Fillet025
  expr: .Placement.Base.y = -1 * (<<ProjectSettings>>.BarLength - <<ProjectSettings>>.WallThickness * 4 - <<ProjectSettings>>.LockingButtonWidth - <<ProjectSettings>>.CrosspinWidth)
  expr: .Placement.Base.z = <<P90Measurements>>.PadWidestWidthOuterShoulderDistanceFromReferencePoint + <<TelescopingBarSettings>>.BarThickness * 2 + <<ProjectSettings>>.TightTolerance
  expr: .Placement.Base.x = -1 * (<<P90Measurements>>.PadWidestWidth / 2 + <<ProjectSettings>>.BarThickness)
FEATURE [Part::Mirroring] Part__Mirroring001  label="Endcap (Mirror #2)"
  Base = (0,0,0)
  Normal = (1,0,0)
  Source = -> Body007
FEATURE [App::Part] Part  label="TelescopingArray"
  Group = -> [Body002,Body008,Body006,Part__Mirroring,Body007,Part__Mirroring001]
  Origin = -> Origin003
  Placement = pos=(0,205,0) rot=(0,0,1;0rad)
